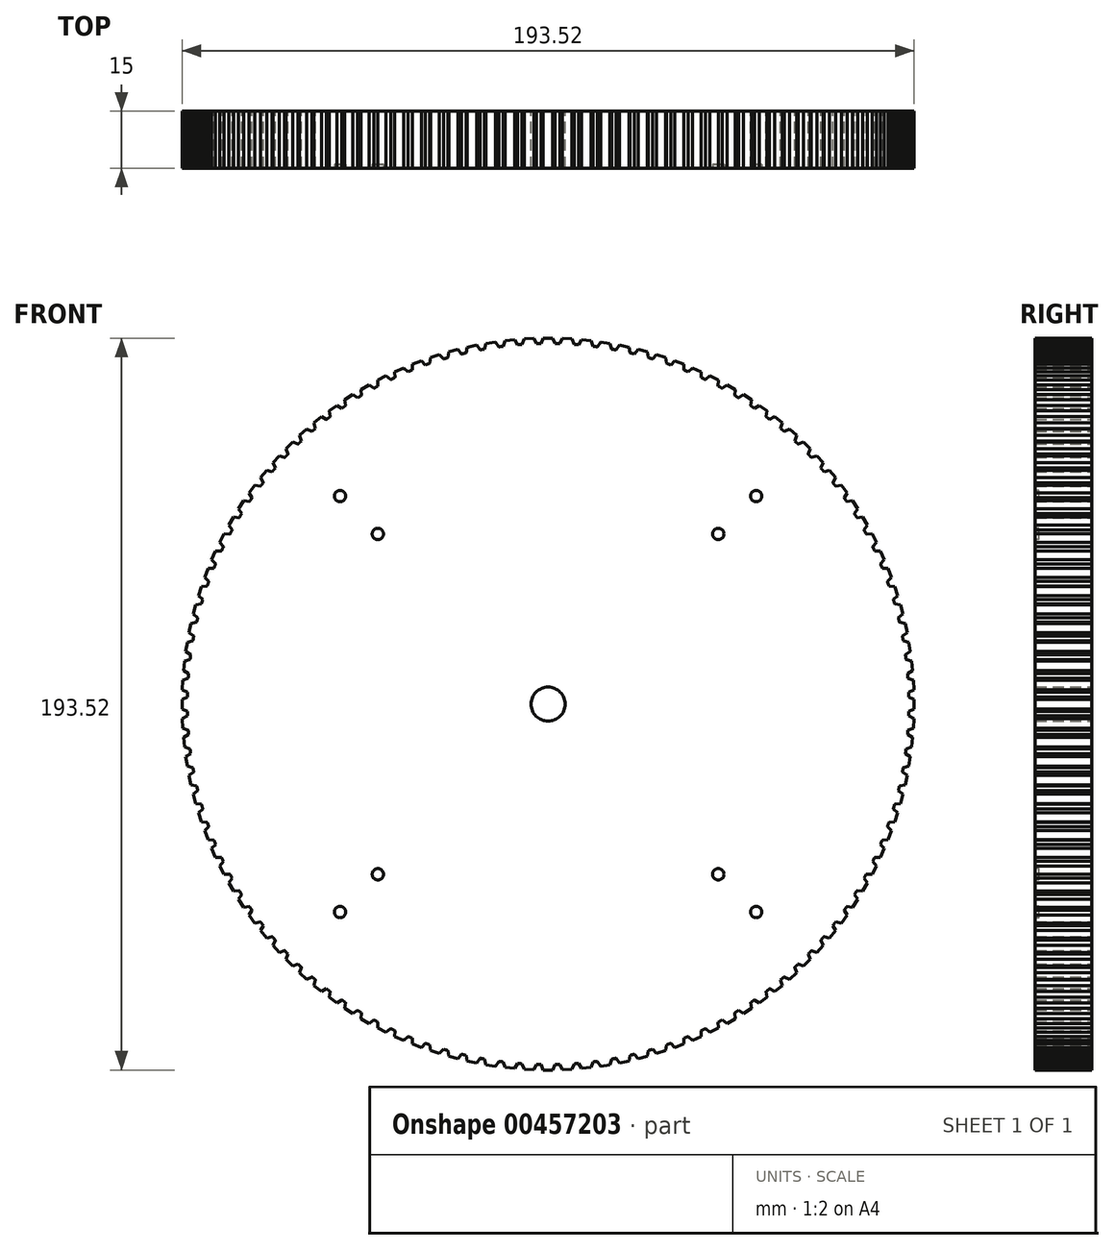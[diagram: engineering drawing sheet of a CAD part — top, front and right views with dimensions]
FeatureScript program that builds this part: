
annotation { "Feature Type Name" : "Feature", "Feature Type Description" : "" }
export const myFeature = defineFeature(function(context is Context, id is Id, definition is map)
    precondition{}
    {
        {
            var Q0;
            Q0=qCreatedBy(makeId("Front.planeOp"),FACE);
            var sketch = newSketch(context, id + "F0", { "sketchPlane" : qUnion([Q0])});
            skCircle(sketch, "E0", {"center": v(0, 0) * mm, "radius": 96.77 * mm, "construction": true});
            skLineSegment(sketch, "E1", {"start": v(0, 96.77) * mm, "end": v(0, 95.37) * mm, "construction": true});
            skCircle(sketch, "E2", {"center": v(0, 0) * mm, "radius": 95.37 * mm});
            skLineSegment(sketch, "E3", {"start": v(0, 0) * mm, "end": v(-1.27, 96.76) * mm, "construction": true});
            skLineSegment(sketch, "E4", {"start": v(0, 0) * mm, "end": v(-2.53, 96.73) * mm, "construction": true});
            skLineSegment(sketch, "E5.MirrorCS", {"start": v(0, 0) * mm, "end": v(1.27, 96.76) * mm, "construction": true});
            skLineSegment(sketch, "E6.MirrorCS", {"start": v(0, 0) * mm, "end": v(2.53, 96.73) * mm, "construction": true});
            skLineSegment(sketch, "E7", {"start": v(-1.27, 96.76) * mm, "end": v(1.27, 96.76) * mm});
            skLineSegment(sketch, "E8", {"start": v(-1.27, 96.76) * mm, "end": v(-1.88, 95.35) * mm});
            skLineSegment(sketch, "E9.MirrorCS", {"start": v(1.27, 96.76) * mm, "end": v(1.88, 95.35) * mm});
            skLineSegment(sketch, "E10.1.0", {"start": v(-6.33, 96.56) * mm, "end": v(-6.87, 95.12) * mm});
            skLineSegment(sketch, "E10.1.1", {"start": v(-6.33, 96.56) * mm, "end": v(-3.8, 96.7) * mm});
            skLineSegment(sketch, "E10.1.2", {"start": v(-3.8, 96.7) * mm, "end": v(-3.11, 95.31) * mm});
            skLineSegment(sketch, "E10.2.0", {"start": v(-11.37, 96.1) * mm, "end": v(-11.84, 94.63) * mm});
            skLineSegment(sketch, "E10.2.1", {"start": v(-11.37, 96.1) * mm, "end": v(-8.85, 96.36) * mm});
            skLineSegment(sketch, "E10.2.2", {"start": v(-8.85, 96.36) * mm, "end": v(-8.1, 95.02) * mm});
            skLineSegment(sketch, "E10.3.0", {"start": v(-16.39, 95.37) * mm, "end": v(-16.77, 93.88) * mm});
            skLineSegment(sketch, "E10.3.1", {"start": v(-16.39, 95.37) * mm, "end": v(-13.89, 95.76) * mm});
            skLineSegment(sketch, "E10.3.2", {"start": v(-13.89, 95.76) * mm, "end": v(-13.06, 94.47) * mm});
            skLineSegment(sketch, "E10.4.0", {"start": v(-21.36, 94.38) * mm, "end": v(-21.66, 92.87) * mm});
            skLineSegment(sketch, "E10.4.1", {"start": v(-21.36, 94.38) * mm, "end": v(-18.88, 94.9) * mm});
            skLineSegment(sketch, "E10.4.2", {"start": v(-18.88, 94.9) * mm, "end": v(-17.98, 93.65) * mm});
            skLineSegment(sketch, "E10.5.0", {"start": v(-26.27, 93.13) * mm, "end": v(-26.5, 91.61) * mm});
            skLineSegment(sketch, "E10.5.1", {"start": v(-26.27, 93.13) * mm, "end": v(-23.82, 93.79) * mm});
            skLineSegment(sketch, "E10.5.2", {"start": v(-23.82, 93.79) * mm, "end": v(-22.86, 92.58) * mm});
            skLineSegment(sketch, "E10.6.0", {"start": v(-31.1, 91.63) * mm, "end": v(-31.25, 90.1) * mm});
            skLineSegment(sketch, "E10.6.1", {"start": v(-31.1, 91.63) * mm, "end": v(-28.7, 92.41) * mm});
            skLineSegment(sketch, "E10.6.2", {"start": v(-28.7, 92.41) * mm, "end": v(-27.68, 91.26) * mm});
            skLineSegment(sketch, "E10.7.0", {"start": v(-35.86, 89.88) * mm, "end": v(-35.92, 88.34) * mm});
            skLineSegment(sketch, "E10.7.1", {"start": v(-35.86, 89.88) * mm, "end": v(-33.5, 90.78) * mm});
            skLineSegment(sketch, "E10.7.2", {"start": v(-33.5, 90.78) * mm, "end": v(-32.41, 89.69) * mm});
            skLineSegment(sketch, "E10.8.0", {"start": v(-40.51, 87.88) * mm, "end": v(-40.5, 86.34) * mm});
            skLineSegment(sketch, "E10.8.1", {"start": v(-40.51, 87.88) * mm, "end": v(-38.2, 88.9) * mm});
            skLineSegment(sketch, "E10.8.2", {"start": v(-38.2, 88.9) * mm, "end": v(-37.06, 87.87) * mm});
            skLineSegment(sketch, "E10.9.0", {"start": v(-45.06, 85.64) * mm, "end": v(-44.96, 84.1) * mm});
            skLineSegment(sketch, "E10.9.1", {"start": v(-45.06, 85.64) * mm, "end": v(-42.8, 86.79) * mm});
            skLineSegment(sketch, "E10.9.2", {"start": v(-42.8, 86.79) * mm, "end": v(-41.61, 85.8) * mm});
            skLineSegment(sketch, "E11", {"start": v(0, 0) * mm, "end": v(0, 96.77) * mm, "construction": true});
            skLineSegment(sketch, "E12.2.10.0", {"start": v(-49.48, 83.16) * mm, "end": v(-49.3, 81.63) * mm});
            skLineSegment(sketch, "E12.3.10.0", {"start": v(-49.48, 83.16) * mm, "end": v(-47.28, 84.43) * mm});
            skLineSegment(sketch, "E12.6.10.0", {"start": v(-47.28, 84.43) * mm, "end": v(-46.05, 83.51) * mm});
            skLineSegment(sketch, "E12.2.11.0", {"start": v(-53.76, 80.46) * mm, "end": v(-53.5, 78.94) * mm});
            skLineSegment(sketch, "E12.3.11.0", {"start": v(-53.76, 80.46) * mm, "end": v(-51.64, 81.84) * mm});
            skLineSegment(sketch, "E12.6.11.0", {"start": v(-51.64, 81.84) * mm, "end": v(-50.35, 80.99) * mm});
            skLineSegment(sketch, "E12.2.12.0", {"start": v(-57.9, 77.53) * mm, "end": v(-57.56, 76.03) * mm});
            skLineSegment(sketch, "E12.3.12.0", {"start": v(-57.9, 77.53) * mm, "end": v(-55.85, 79.02) * mm});
            skLineSegment(sketch, "E12.6.12.0", {"start": v(-55.85, 79.02) * mm, "end": v(-54.52, 78.24) * mm});
            skLineSegment(sketch, "E12.2.13.0", {"start": v(-61.88, 74.4) * mm, "end": v(-61.46, 72.92) * mm});
            skLineSegment(sketch, "E12.3.13.0", {"start": v(-61.88, 74.4) * mm, "end": v(-59.9, 76) * mm});
            skLineSegment(sketch, "E12.6.13.0", {"start": v(-59.9, 76) * mm, "end": v(-58.54, 75.28) * mm});
            skLineSegment(sketch, "E12.2.14.0", {"start": v(-65.68, 71.06) * mm, "end": v(-65.2, 69.6) * mm});
            skLineSegment(sketch, "E12.3.14.0", {"start": v(-65.68, 71.06) * mm, "end": v(-63.8, 72.75) * mm});
            skLineSegment(sketch, "E12.6.14.0", {"start": v(-63.8, 72.75) * mm, "end": v(-62.4, 72.11) * mm});
            skLineSegment(sketch, "E12.2.15.0", {"start": v(-69.31, 67.52) * mm, "end": v(-68.75, 66.1) * mm});
            skLineSegment(sketch, "E12.3.15.0", {"start": v(-69.31, 67.52) * mm, "end": v(-67.52, 69.31) * mm});
            skLineSegment(sketch, "E12.6.15.0", {"start": v(-67.52, 69.31) * mm, "end": v(-66.1, 68.75) * mm});
            skLineSegment(sketch, "E12.2.16.0", {"start": v(-72.75, 63.8) * mm, "end": v(-72.11, 62.4) * mm});
            skLineSegment(sketch, "E12.3.16.0", {"start": v(-72.75, 63.8) * mm, "end": v(-71.06, 65.68) * mm});
            skLineSegment(sketch, "E12.6.16.0", {"start": v(-71.06, 65.68) * mm, "end": v(-69.6, 65.2) * mm});
            skLineSegment(sketch, "E12.2.17.0", {"start": v(-76, 59.9) * mm, "end": v(-75.28, 58.54) * mm});
            skLineSegment(sketch, "E12.3.17.0", {"start": v(-76, 59.9) * mm, "end": v(-74.4, 61.88) * mm});
            skLineSegment(sketch, "E12.6.17.0", {"start": v(-74.4, 61.88) * mm, "end": v(-72.92, 61.46) * mm});
            skLineSegment(sketch, "E12.2.18.0", {"start": v(-79.02, 55.85) * mm, "end": v(-78.24, 54.52) * mm});
            skLineSegment(sketch, "E12.3.18.0", {"start": v(-79.02, 55.85) * mm, "end": v(-77.53, 57.9) * mm});
            skLineSegment(sketch, "E12.6.18.0", {"start": v(-77.53, 57.9) * mm, "end": v(-76.03, 57.56) * mm});
            skLineSegment(sketch, "E12.2.19.0", {"start": v(-81.84, 51.64) * mm, "end": v(-80.99, 50.35) * mm});
            skLineSegment(sketch, "E12.3.19.0", {"start": v(-81.84, 51.64) * mm, "end": v(-80.46, 53.76) * mm});
            skLineSegment(sketch, "E12.6.19.0", {"start": v(-80.46, 53.76) * mm, "end": v(-78.94, 53.5) * mm});
            skLineSegment(sketch, "E12.2.20.0", {"start": v(-84.43, 47.28) * mm, "end": v(-83.51, 46.05) * mm});
            skLineSegment(sketch, "E12.3.20.0", {"start": v(-84.43, 47.28) * mm, "end": v(-83.16, 49.48) * mm});
            skLineSegment(sketch, "E12.6.20.0", {"start": v(-83.16, 49.48) * mm, "end": v(-81.63, 49.3) * mm});
            skLineSegment(sketch, "E12.2.21.0", {"start": v(-86.79, 42.8) * mm, "end": v(-85.8, 41.61) * mm});
            skLineSegment(sketch, "E12.3.21.0", {"start": v(-86.79, 42.8) * mm, "end": v(-85.64, 45.06) * mm});
            skLineSegment(sketch, "E12.6.21.0", {"start": v(-85.64, 45.06) * mm, "end": v(-84.1, 44.96) * mm});
            skLineSegment(sketch, "E12.2.22.0", {"start": v(-88.9, 38.2) * mm, "end": v(-87.87, 37.06) * mm});
            skLineSegment(sketch, "E12.3.22.0", {"start": v(-88.9, 38.2) * mm, "end": v(-87.88, 40.51) * mm});
            skLineSegment(sketch, "E12.6.22.0", {"start": v(-87.88, 40.51) * mm, "end": v(-86.34, 40.5) * mm});
            skLineSegment(sketch, "E12.2.23.0", {"start": v(-90.78, 33.5) * mm, "end": v(-89.69, 32.41) * mm});
            skLineSegment(sketch, "E12.3.23.0", {"start": v(-90.78, 33.5) * mm, "end": v(-89.88, 35.86) * mm});
            skLineSegment(sketch, "E12.6.23.0", {"start": v(-89.88, 35.86) * mm, "end": v(-88.34, 35.92) * mm});
            skLineSegment(sketch, "E12.2.24.0", {"start": v(-92.41, 28.7) * mm, "end": v(-91.26, 27.68) * mm});
            skLineSegment(sketch, "E12.3.24.0", {"start": v(-92.41, 28.7) * mm, "end": v(-91.63, 31.1) * mm});
            skLineSegment(sketch, "E12.6.24.0", {"start": v(-91.63, 31.1) * mm, "end": v(-90.1, 31.25) * mm});
            skLineSegment(sketch, "E12.2.25.0", {"start": v(-93.79, 23.82) * mm, "end": v(-92.58, 22.86) * mm});
            skLineSegment(sketch, "E12.3.25.0", {"start": v(-93.79, 23.82) * mm, "end": v(-93.13, 26.27) * mm});
            skLineSegment(sketch, "E12.6.25.0", {"start": v(-93.13, 26.27) * mm, "end": v(-91.61, 26.5) * mm});
            skLineSegment(sketch, "E12.2.26.0", {"start": v(-94.9, 18.88) * mm, "end": v(-93.65, 17.98) * mm});
            skLineSegment(sketch, "E12.3.26.0", {"start": v(-94.9, 18.88) * mm, "end": v(-94.38, 21.36) * mm});
            skLineSegment(sketch, "E12.6.26.0", {"start": v(-94.38, 21.36) * mm, "end": v(-92.87, 21.66) * mm});
            skLineSegment(sketch, "E12.2.27.0", {"start": v(-95.76, 13.89) * mm, "end": v(-94.47, 13.06) * mm});
            skLineSegment(sketch, "E12.3.27.0", {"start": v(-95.76, 13.89) * mm, "end": v(-95.37, 16.39) * mm});
            skLineSegment(sketch, "E12.6.27.0", {"start": v(-95.37, 16.39) * mm, "end": v(-93.88, 16.77) * mm});
            skLineSegment(sketch, "E12.2.28.0", {"start": v(-96.36, 8.85) * mm, "end": v(-95.02, 8.1) * mm});
            skLineSegment(sketch, "E12.3.28.0", {"start": v(-96.36, 8.85) * mm, "end": v(-96.1, 11.37) * mm});
            skLineSegment(sketch, "E12.6.28.0", {"start": v(-96.1, 11.37) * mm, "end": v(-94.63, 11.84) * mm});
            skLineSegment(sketch, "E12.2.29.0", {"start": v(-96.7, 3.8) * mm, "end": v(-95.31, 3.11) * mm});
            skLineSegment(sketch, "E12.3.29.0", {"start": v(-96.7, 3.8) * mm, "end": v(-96.56, 6.33) * mm});
            skLineSegment(sketch, "E12.6.29.0", {"start": v(-96.56, 6.33) * mm, "end": v(-95.12, 6.87) * mm});
            skLineSegment(sketch, "E12.2.30.0", {"start": v(-96.76, -1.27) * mm, "end": v(-95.35, -1.88) * mm});
            skLineSegment(sketch, "E12.3.30.0", {"start": v(-96.76, -1.27) * mm, "end": v(-96.76, 1.27) * mm});
            skLineSegment(sketch, "E12.6.30.0", {"start": v(-96.76, 1.27) * mm, "end": v(-95.35, 1.88) * mm});
            skLineSegment(sketch, "E12.2.31.0", {"start": v(-96.56, -6.33) * mm, "end": v(-95.12, -6.87) * mm});
            skLineSegment(sketch, "E12.3.31.0", {"start": v(-96.56, -6.33) * mm, "end": v(-96.7, -3.8) * mm});
            skLineSegment(sketch, "E12.6.31.0", {"start": v(-96.7, -3.8) * mm, "end": v(-95.31, -3.11) * mm});
            skLineSegment(sketch, "E12.2.32.0", {"start": v(-96.1, -11.37) * mm, "end": v(-94.63, -11.84) * mm});
            skLineSegment(sketch, "E12.3.32.0", {"start": v(-96.1, -11.37) * mm, "end": v(-96.36, -8.85) * mm});
            skLineSegment(sketch, "E12.6.32.0", {"start": v(-96.36, -8.85) * mm, "end": v(-95.02, -8.1) * mm});
            skLineSegment(sketch, "E12.2.33.0", {"start": v(-95.37, -16.39) * mm, "end": v(-93.88, -16.77) * mm});
            skLineSegment(sketch, "E12.3.33.0", {"start": v(-95.37, -16.39) * mm, "end": v(-95.76, -13.89) * mm});
            skLineSegment(sketch, "E12.6.33.0", {"start": v(-95.76, -13.89) * mm, "end": v(-94.47, -13.06) * mm});
            skLineSegment(sketch, "E12.2.34.0", {"start": v(-94.38, -21.36) * mm, "end": v(-92.87, -21.66) * mm});
            skLineSegment(sketch, "E12.3.34.0", {"start": v(-94.38, -21.36) * mm, "end": v(-94.9, -18.88) * mm});
            skLineSegment(sketch, "E12.6.34.0", {"start": v(-94.9, -18.88) * mm, "end": v(-93.65, -17.98) * mm});
            skLineSegment(sketch, "E12.2.35.0", {"start": v(-93.13, -26.27) * mm, "end": v(-91.61, -26.5) * mm});
            skLineSegment(sketch, "E12.3.35.0", {"start": v(-93.13, -26.27) * mm, "end": v(-93.79, -23.82) * mm});
            skLineSegment(sketch, "E12.6.35.0", {"start": v(-93.79, -23.82) * mm, "end": v(-92.58, -22.86) * mm});
            skLineSegment(sketch, "E12.2.36.0", {"start": v(-91.63, -31.1) * mm, "end": v(-90.1, -31.25) * mm});
            skLineSegment(sketch, "E12.3.36.0", {"start": v(-91.63, -31.1) * mm, "end": v(-92.41, -28.7) * mm});
            skLineSegment(sketch, "E12.6.36.0", {"start": v(-92.41, -28.7) * mm, "end": v(-91.26, -27.68) * mm});
            skLineSegment(sketch, "E12.2.37.0", {"start": v(-89.88, -35.86) * mm, "end": v(-88.34, -35.92) * mm});
            skLineSegment(sketch, "E12.3.37.0", {"start": v(-89.88, -35.86) * mm, "end": v(-90.78, -33.5) * mm});
            skLineSegment(sketch, "E12.6.37.0", {"start": v(-90.78, -33.5) * mm, "end": v(-89.69, -32.41) * mm});
            skLineSegment(sketch, "E12.2.38.0", {"start": v(-87.88, -40.51) * mm, "end": v(-86.34, -40.5) * mm});
            skLineSegment(sketch, "E12.3.38.0", {"start": v(-87.88, -40.51) * mm, "end": v(-88.9, -38.2) * mm});
            skLineSegment(sketch, "E12.6.38.0", {"start": v(-88.9, -38.2) * mm, "end": v(-87.87, -37.06) * mm});
            skLineSegment(sketch, "E12.2.39.0", {"start": v(-85.64, -45.06) * mm, "end": v(-84.1, -44.96) * mm});
            skLineSegment(sketch, "E12.3.39.0", {"start": v(-85.64, -45.06) * mm, "end": v(-86.79, -42.8) * mm});
            skLineSegment(sketch, "E12.6.39.0", {"start": v(-86.79, -42.8) * mm, "end": v(-85.8, -41.61) * mm});
            skLineSegment(sketch, "E12.2.40.0", {"start": v(-83.16, -49.48) * mm, "end": v(-81.63, -49.3) * mm});
            skLineSegment(sketch, "E12.3.40.0", {"start": v(-83.16, -49.48) * mm, "end": v(-84.43, -47.28) * mm});
            skLineSegment(sketch, "E12.6.40.0", {"start": v(-84.43, -47.28) * mm, "end": v(-83.51, -46.05) * mm});
            skLineSegment(sketch, "E12.2.41.0", {"start": v(-80.46, -53.76) * mm, "end": v(-78.94, -53.5) * mm});
            skLineSegment(sketch, "E12.3.41.0", {"start": v(-80.46, -53.76) * mm, "end": v(-81.84, -51.64) * mm});
            skLineSegment(sketch, "E12.6.41.0", {"start": v(-81.84, -51.64) * mm, "end": v(-80.99, -50.35) * mm});
            skLineSegment(sketch, "E12.2.42.0", {"start": v(-77.53, -57.9) * mm, "end": v(-76.03, -57.56) * mm});
            skLineSegment(sketch, "E12.3.42.0", {"start": v(-77.53, -57.9) * mm, "end": v(-79.02, -55.85) * mm});
            skLineSegment(sketch, "E12.6.42.0", {"start": v(-79.02, -55.85) * mm, "end": v(-78.24, -54.52) * mm});
            skLineSegment(sketch, "E12.2.43.0", {"start": v(-74.4, -61.88) * mm, "end": v(-72.92, -61.46) * mm});
            skLineSegment(sketch, "E12.3.43.0", {"start": v(-74.4, -61.88) * mm, "end": v(-76, -59.9) * mm});
            skLineSegment(sketch, "E12.6.43.0", {"start": v(-76, -59.9) * mm, "end": v(-75.28, -58.54) * mm});
            skLineSegment(sketch, "E12.2.44.0", {"start": v(-71.06, -65.68) * mm, "end": v(-69.6, -65.2) * mm});
            skLineSegment(sketch, "E12.3.44.0", {"start": v(-71.06, -65.68) * mm, "end": v(-72.75, -63.8) * mm});
            skLineSegment(sketch, "E12.6.44.0", {"start": v(-72.75, -63.8) * mm, "end": v(-72.11, -62.4) * mm});
            skLineSegment(sketch, "E12.2.45.0", {"start": v(-67.52, -69.31) * mm, "end": v(-66.1, -68.75) * mm});
            skLineSegment(sketch, "E12.3.45.0", {"start": v(-67.52, -69.31) * mm, "end": v(-69.31, -67.52) * mm});
            skLineSegment(sketch, "E12.6.45.0", {"start": v(-69.31, -67.52) * mm, "end": v(-68.75, -66.1) * mm});
            skLineSegment(sketch, "E12.2.46.0", {"start": v(-63.8, -72.75) * mm, "end": v(-62.4, -72.11) * mm});
            skLineSegment(sketch, "E12.3.46.0", {"start": v(-63.8, -72.75) * mm, "end": v(-65.68, -71.06) * mm});
            skLineSegment(sketch, "E12.6.46.0", {"start": v(-65.68, -71.06) * mm, "end": v(-65.2, -69.6) * mm});
            skLineSegment(sketch, "E12.2.47.0", {"start": v(-59.9, -76) * mm, "end": v(-58.54, -75.28) * mm});
            skLineSegment(sketch, "E12.3.47.0", {"start": v(-59.9, -76) * mm, "end": v(-61.88, -74.4) * mm});
            skLineSegment(sketch, "E12.6.47.0", {"start": v(-61.88, -74.4) * mm, "end": v(-61.46, -72.92) * mm});
            skLineSegment(sketch, "E12.2.48.0", {"start": v(-55.85, -79.02) * mm, "end": v(-54.52, -78.24) * mm});
            skLineSegment(sketch, "E12.3.48.0", {"start": v(-55.85, -79.02) * mm, "end": v(-57.9, -77.53) * mm});
            skLineSegment(sketch, "E12.6.48.0", {"start": v(-57.9, -77.53) * mm, "end": v(-57.56, -76.03) * mm});
            skLineSegment(sketch, "E12.2.49.0", {"start": v(-51.64, -81.84) * mm, "end": v(-50.35, -80.99) * mm});
            skLineSegment(sketch, "E12.3.49.0", {"start": v(-51.64, -81.84) * mm, "end": v(-53.76, -80.46) * mm});
            skLineSegment(sketch, "E12.6.49.0", {"start": v(-53.76, -80.46) * mm, "end": v(-53.5, -78.94) * mm});
            skLineSegment(sketch, "E12.2.50.0", {"start": v(-47.28, -84.43) * mm, "end": v(-46.05, -83.51) * mm});
            skLineSegment(sketch, "E12.3.50.0", {"start": v(-47.28, -84.43) * mm, "end": v(-49.48, -83.16) * mm});
            skLineSegment(sketch, "E12.6.50.0", {"start": v(-49.48, -83.16) * mm, "end": v(-49.3, -81.63) * mm});
            skLineSegment(sketch, "E12.2.51.0", {"start": v(-42.8, -86.79) * mm, "end": v(-41.61, -85.8) * mm});
            skLineSegment(sketch, "E12.3.51.0", {"start": v(-42.8, -86.79) * mm, "end": v(-45.06, -85.64) * mm});
            skLineSegment(sketch, "E12.6.51.0", {"start": v(-45.06, -85.64) * mm, "end": v(-44.96, -84.1) * mm});
            skLineSegment(sketch, "E12.2.52.0", {"start": v(-38.2, -88.9) * mm, "end": v(-37.06, -87.87) * mm});
            skLineSegment(sketch, "E12.3.52.0", {"start": v(-38.2, -88.9) * mm, "end": v(-40.51, -87.88) * mm});
            skLineSegment(sketch, "E12.6.52.0", {"start": v(-40.51, -87.88) * mm, "end": v(-40.5, -86.34) * mm});
            skLineSegment(sketch, "E12.2.53.0", {"start": v(-33.5, -90.78) * mm, "end": v(-32.41, -89.69) * mm});
            skLineSegment(sketch, "E12.3.53.0", {"start": v(-33.5, -90.78) * mm, "end": v(-35.86, -89.88) * mm});
            skLineSegment(sketch, "E12.6.53.0", {"start": v(-35.86, -89.88) * mm, "end": v(-35.92, -88.34) * mm});
            skLineSegment(sketch, "E12.2.54.0", {"start": v(-28.7, -92.41) * mm, "end": v(-27.68, -91.26) * mm});
            skLineSegment(sketch, "E12.3.54.0", {"start": v(-28.7, -92.41) * mm, "end": v(-31.1, -91.63) * mm});
            skLineSegment(sketch, "E12.6.54.0", {"start": v(-31.1, -91.63) * mm, "end": v(-31.25, -90.1) * mm});
            skLineSegment(sketch, "E12.2.55.0", {"start": v(-23.82, -93.79) * mm, "end": v(-22.86, -92.58) * mm});
            skLineSegment(sketch, "E12.3.55.0", {"start": v(-23.82, -93.79) * mm, "end": v(-26.27, -93.13) * mm});
            skLineSegment(sketch, "E12.6.55.0", {"start": v(-26.27, -93.13) * mm, "end": v(-26.5, -91.61) * mm});
            skLineSegment(sketch, "E12.2.56.0", {"start": v(-18.88, -94.9) * mm, "end": v(-17.98, -93.65) * mm});
            skLineSegment(sketch, "E12.3.56.0", {"start": v(-18.88, -94.9) * mm, "end": v(-21.36, -94.38) * mm});
            skLineSegment(sketch, "E12.6.56.0", {"start": v(-21.36, -94.38) * mm, "end": v(-21.66, -92.87) * mm});
            skLineSegment(sketch, "E12.2.57.0", {"start": v(-13.89, -95.76) * mm, "end": v(-13.06, -94.47) * mm});
            skLineSegment(sketch, "E12.3.57.0", {"start": v(-13.89, -95.76) * mm, "end": v(-16.39, -95.37) * mm});
            skLineSegment(sketch, "E12.6.57.0", {"start": v(-16.39, -95.37) * mm, "end": v(-16.77, -93.88) * mm});
            skLineSegment(sketch, "E12.2.58.0", {"start": v(-8.85, -96.36) * mm, "end": v(-8.1, -95.02) * mm});
            skLineSegment(sketch, "E12.3.58.0", {"start": v(-8.85, -96.36) * mm, "end": v(-11.37, -96.1) * mm});
            skLineSegment(sketch, "E12.6.58.0", {"start": v(-11.37, -96.1) * mm, "end": v(-11.84, -94.63) * mm});
            skLineSegment(sketch, "E12.2.59.0", {"start": v(-3.8, -96.7) * mm, "end": v(-3.11, -95.31) * mm});
            skLineSegment(sketch, "E12.3.59.0", {"start": v(-3.8, -96.7) * mm, "end": v(-6.33, -96.56) * mm});
            skLineSegment(sketch, "E12.6.59.0", {"start": v(-6.33, -96.56) * mm, "end": v(-6.87, -95.12) * mm});
            skLineSegment(sketch, "E13.2.60.0", {"start": v(1.27, -96.76) * mm, "end": v(1.88, -95.35) * mm});
            skLineSegment(sketch, "E13.3.60.0", {"start": v(1.27, -96.76) * mm, "end": v(-1.27, -96.76) * mm});
            skLineSegment(sketch, "E13.6.60.0", {"start": v(-1.27, -96.76) * mm, "end": v(-1.88, -95.35) * mm});
            skLineSegment(sketch, "E13.2.61.0", {"start": v(6.33, -96.56) * mm, "end": v(6.87, -95.12) * mm});
            skLineSegment(sketch, "E13.3.61.0", {"start": v(6.33, -96.56) * mm, "end": v(3.8, -96.7) * mm});
            skLineSegment(sketch, "E13.6.61.0", {"start": v(3.8, -96.7) * mm, "end": v(3.11, -95.31) * mm});
            skLineSegment(sketch, "E13.2.62.0", {"start": v(11.37, -96.1) * mm, "end": v(11.84, -94.63) * mm});
            skLineSegment(sketch, "E13.3.62.0", {"start": v(11.37, -96.1) * mm, "end": v(8.85, -96.36) * mm});
            skLineSegment(sketch, "E13.6.62.0", {"start": v(8.85, -96.36) * mm, "end": v(8.1, -95.02) * mm});
            skLineSegment(sketch, "E13.2.63.0", {"start": v(16.39, -95.37) * mm, "end": v(16.77, -93.88) * mm});
            skLineSegment(sketch, "E13.3.63.0", {"start": v(16.39, -95.37) * mm, "end": v(13.89, -95.76) * mm});
            skLineSegment(sketch, "E13.6.63.0", {"start": v(13.89, -95.76) * mm, "end": v(13.06, -94.47) * mm});
            skLineSegment(sketch, "E13.2.64.0", {"start": v(21.36, -94.38) * mm, "end": v(21.66, -92.87) * mm});
            skLineSegment(sketch, "E13.3.64.0", {"start": v(21.36, -94.38) * mm, "end": v(18.88, -94.9) * mm});
            skLineSegment(sketch, "E13.6.64.0", {"start": v(18.88, -94.9) * mm, "end": v(17.98, -93.65) * mm});
            skLineSegment(sketch, "E13.2.65.0", {"start": v(26.27, -93.13) * mm, "end": v(26.5, -91.61) * mm});
            skLineSegment(sketch, "E13.3.65.0", {"start": v(26.27, -93.13) * mm, "end": v(23.82, -93.79) * mm});
            skLineSegment(sketch, "E13.6.65.0", {"start": v(23.82, -93.79) * mm, "end": v(22.86, -92.58) * mm});
            skLineSegment(sketch, "E13.2.66.0", {"start": v(31.1, -91.63) * mm, "end": v(31.25, -90.1) * mm});
            skLineSegment(sketch, "E13.3.66.0", {"start": v(31.1, -91.63) * mm, "end": v(28.7, -92.41) * mm});
            skLineSegment(sketch, "E13.6.66.0", {"start": v(28.7, -92.41) * mm, "end": v(27.68, -91.26) * mm});
            skLineSegment(sketch, "E13.2.67.0", {"start": v(35.86, -89.88) * mm, "end": v(35.92, -88.34) * mm});
            skLineSegment(sketch, "E13.3.67.0", {"start": v(35.86, -89.88) * mm, "end": v(33.5, -90.78) * mm});
            skLineSegment(sketch, "E13.6.67.0", {"start": v(33.5, -90.78) * mm, "end": v(32.41, -89.69) * mm});
            skLineSegment(sketch, "E13.2.68.0", {"start": v(40.51, -87.88) * mm, "end": v(40.5, -86.34) * mm});
            skLineSegment(sketch, "E13.3.68.0", {"start": v(40.51, -87.88) * mm, "end": v(38.2, -88.9) * mm});
            skLineSegment(sketch, "E13.6.68.0", {"start": v(38.2, -88.9) * mm, "end": v(37.06, -87.87) * mm});
            skLineSegment(sketch, "E13.2.69.0", {"start": v(45.06, -85.64) * mm, "end": v(44.96, -84.1) * mm});
            skLineSegment(sketch, "E13.3.69.0", {"start": v(45.06, -85.64) * mm, "end": v(42.8, -86.79) * mm});
            skLineSegment(sketch, "E13.6.69.0", {"start": v(42.8, -86.79) * mm, "end": v(41.61, -85.8) * mm});
            skLineSegment(sketch, "E13.2.70.0", {"start": v(49.48, -83.16) * mm, "end": v(49.3, -81.63) * mm});
            skLineSegment(sketch, "E13.3.70.0", {"start": v(49.48, -83.16) * mm, "end": v(47.28, -84.43) * mm});
            skLineSegment(sketch, "E13.6.70.0", {"start": v(47.28, -84.43) * mm, "end": v(46.05, -83.51) * mm});
            skLineSegment(sketch, "E13.2.71.0", {"start": v(53.76, -80.46) * mm, "end": v(53.5, -78.94) * mm});
            skLineSegment(sketch, "E13.3.71.0", {"start": v(53.76, -80.46) * mm, "end": v(51.64, -81.84) * mm});
            skLineSegment(sketch, "E13.6.71.0", {"start": v(51.64, -81.84) * mm, "end": v(50.35, -80.99) * mm});
            skLineSegment(sketch, "E13.2.72.0", {"start": v(57.9, -77.53) * mm, "end": v(57.56, -76.03) * mm});
            skLineSegment(sketch, "E13.3.72.0", {"start": v(57.9, -77.53) * mm, "end": v(55.85, -79.02) * mm});
            skLineSegment(sketch, "E13.6.72.0", {"start": v(55.85, -79.02) * mm, "end": v(54.52, -78.24) * mm});
            skLineSegment(sketch, "E13.2.73.0", {"start": v(61.88, -74.4) * mm, "end": v(61.46, -72.92) * mm});
            skLineSegment(sketch, "E13.3.73.0", {"start": v(61.88, -74.4) * mm, "end": v(59.9, -76) * mm});
            skLineSegment(sketch, "E13.6.73.0", {"start": v(59.9, -76) * mm, "end": v(58.54, -75.28) * mm});
            skLineSegment(sketch, "E13.2.74.0", {"start": v(65.68, -71.06) * mm, "end": v(65.2, -69.6) * mm});
            skLineSegment(sketch, "E13.3.74.0", {"start": v(65.68, -71.06) * mm, "end": v(63.8, -72.75) * mm});
            skLineSegment(sketch, "E13.6.74.0", {"start": v(63.8, -72.75) * mm, "end": v(62.4, -72.11) * mm});
            skLineSegment(sketch, "E13.2.75.0", {"start": v(69.31, -67.52) * mm, "end": v(68.75, -66.1) * mm});
            skLineSegment(sketch, "E13.3.75.0", {"start": v(69.31, -67.52) * mm, "end": v(67.52, -69.31) * mm});
            skLineSegment(sketch, "E13.6.75.0", {"start": v(67.52, -69.31) * mm, "end": v(66.1, -68.75) * mm});
            skLineSegment(sketch, "E13.2.76.0", {"start": v(72.75, -63.8) * mm, "end": v(72.11, -62.4) * mm});
            skLineSegment(sketch, "E13.3.76.0", {"start": v(72.75, -63.8) * mm, "end": v(71.06, -65.68) * mm});
            skLineSegment(sketch, "E13.6.76.0", {"start": v(71.06, -65.68) * mm, "end": v(69.6, -65.2) * mm});
            skLineSegment(sketch, "E13.2.77.0", {"start": v(76, -59.9) * mm, "end": v(75.28, -58.54) * mm});
            skLineSegment(sketch, "E13.3.77.0", {"start": v(76, -59.9) * mm, "end": v(74.4, -61.88) * mm});
            skLineSegment(sketch, "E13.6.77.0", {"start": v(74.4, -61.88) * mm, "end": v(72.92, -61.46) * mm});
            skLineSegment(sketch, "E13.2.78.0", {"start": v(79.02, -55.85) * mm, "end": v(78.24, -54.52) * mm});
            skLineSegment(sketch, "E13.3.78.0", {"start": v(79.02, -55.85) * mm, "end": v(77.53, -57.9) * mm});
            skLineSegment(sketch, "E13.6.78.0", {"start": v(77.53, -57.9) * mm, "end": v(76.03, -57.56) * mm});
            skLineSegment(sketch, "E13.2.79.0", {"start": v(81.84, -51.64) * mm, "end": v(80.99, -50.35) * mm});
            skLineSegment(sketch, "E13.3.79.0", {"start": v(81.84, -51.64) * mm, "end": v(80.46, -53.76) * mm});
            skLineSegment(sketch, "E13.6.79.0", {"start": v(80.46, -53.76) * mm, "end": v(78.94, -53.5) * mm});
            skLineSegment(sketch, "E13.2.80.0", {"start": v(84.43, -47.28) * mm, "end": v(83.51, -46.05) * mm});
            skLineSegment(sketch, "E13.3.80.0", {"start": v(84.43, -47.28) * mm, "end": v(83.16, -49.48) * mm});
            skLineSegment(sketch, "E13.6.80.0", {"start": v(83.16, -49.48) * mm, "end": v(81.63, -49.3) * mm});
            skLineSegment(sketch, "E13.2.81.0", {"start": v(86.79, -42.8) * mm, "end": v(85.8, -41.61) * mm});
            skLineSegment(sketch, "E13.3.81.0", {"start": v(86.79, -42.8) * mm, "end": v(85.64, -45.06) * mm});
            skLineSegment(sketch, "E13.6.81.0", {"start": v(85.64, -45.06) * mm, "end": v(84.1, -44.96) * mm});
            skLineSegment(sketch, "E13.2.82.0", {"start": v(88.9, -38.2) * mm, "end": v(87.87, -37.06) * mm});
            skLineSegment(sketch, "E13.3.82.0", {"start": v(88.9, -38.2) * mm, "end": v(87.88, -40.51) * mm});
            skLineSegment(sketch, "E13.6.82.0", {"start": v(87.88, -40.51) * mm, "end": v(86.34, -40.5) * mm});
            skLineSegment(sketch, "E13.2.83.0", {"start": v(90.78, -33.5) * mm, "end": v(89.69, -32.41) * mm});
            skLineSegment(sketch, "E13.3.83.0", {"start": v(90.78, -33.5) * mm, "end": v(89.88, -35.86) * mm});
            skLineSegment(sketch, "E13.6.83.0", {"start": v(89.88, -35.86) * mm, "end": v(88.34, -35.92) * mm});
            skLineSegment(sketch, "E13.2.84.0", {"start": v(92.41, -28.7) * mm, "end": v(91.26, -27.68) * mm});
            skLineSegment(sketch, "E13.3.84.0", {"start": v(92.41, -28.7) * mm, "end": v(91.63, -31.1) * mm});
            skLineSegment(sketch, "E13.6.84.0", {"start": v(91.63, -31.1) * mm, "end": v(90.1, -31.25) * mm});
            skLineSegment(sketch, "E13.2.85.0", {"start": v(93.79, -23.82) * mm, "end": v(92.58, -22.86) * mm});
            skLineSegment(sketch, "E13.3.85.0", {"start": v(93.79, -23.82) * mm, "end": v(93.13, -26.27) * mm});
            skLineSegment(sketch, "E13.6.85.0", {"start": v(93.13, -26.27) * mm, "end": v(91.61, -26.5) * mm});
            skLineSegment(sketch, "E13.2.86.0", {"start": v(94.9, -18.88) * mm, "end": v(93.65, -17.98) * mm});
            skLineSegment(sketch, "E13.3.86.0", {"start": v(94.9, -18.88) * mm, "end": v(94.38, -21.36) * mm});
            skLineSegment(sketch, "E13.6.86.0", {"start": v(94.38, -21.36) * mm, "end": v(92.87, -21.66) * mm});
            skLineSegment(sketch, "E13.2.87.0", {"start": v(95.76, -13.89) * mm, "end": v(94.47, -13.06) * mm});
            skLineSegment(sketch, "E13.3.87.0", {"start": v(95.76, -13.89) * mm, "end": v(95.37, -16.39) * mm});
            skLineSegment(sketch, "E13.6.87.0", {"start": v(95.37, -16.39) * mm, "end": v(93.88, -16.77) * mm});
            skLineSegment(sketch, "E13.2.88.0", {"start": v(96.36, -8.85) * mm, "end": v(95.02, -8.1) * mm});
            skLineSegment(sketch, "E13.3.88.0", {"start": v(96.36, -8.85) * mm, "end": v(96.1, -11.37) * mm});
            skLineSegment(sketch, "E13.6.88.0", {"start": v(96.1, -11.37) * mm, "end": v(94.63, -11.84) * mm});
            skLineSegment(sketch, "E13.2.89.0", {"start": v(96.7, -3.8) * mm, "end": v(95.31, -3.11) * mm});
            skLineSegment(sketch, "E13.3.89.0", {"start": v(96.7, -3.8) * mm, "end": v(96.56, -6.33) * mm});
            skLineSegment(sketch, "E13.6.89.0", {"start": v(96.56, -6.33) * mm, "end": v(95.12, -6.87) * mm});
            skLineSegment(sketch, "E13.2.90.0", {"start": v(96.76, 1.27) * mm, "end": v(95.35, 1.88) * mm});
            skLineSegment(sketch, "E13.3.90.0", {"start": v(96.76, 1.27) * mm, "end": v(96.76, -1.27) * mm});
            skLineSegment(sketch, "E13.6.90.0", {"start": v(96.76, -1.27) * mm, "end": v(95.35, -1.88) * mm});
            skLineSegment(sketch, "E13.2.91.0", {"start": v(96.56, 6.33) * mm, "end": v(95.12, 6.87) * mm});
            skLineSegment(sketch, "E13.3.91.0", {"start": v(96.56, 6.33) * mm, "end": v(96.7, 3.8) * mm});
            skLineSegment(sketch, "E13.6.91.0", {"start": v(96.7, 3.8) * mm, "end": v(95.31, 3.11) * mm});
            skLineSegment(sketch, "E13.2.92.0", {"start": v(96.1, 11.37) * mm, "end": v(94.63, 11.84) * mm});
            skLineSegment(sketch, "E13.3.92.0", {"start": v(96.1, 11.37) * mm, "end": v(96.36, 8.85) * mm});
            skLineSegment(sketch, "E13.6.92.0", {"start": v(96.36, 8.85) * mm, "end": v(95.02, 8.1) * mm});
            skLineSegment(sketch, "E13.2.93.0", {"start": v(95.37, 16.39) * mm, "end": v(93.88, 16.77) * mm});
            skLineSegment(sketch, "E13.3.93.0", {"start": v(95.37, 16.39) * mm, "end": v(95.76, 13.89) * mm});
            skLineSegment(sketch, "E13.6.93.0", {"start": v(95.76, 13.89) * mm, "end": v(94.47, 13.06) * mm});
            skLineSegment(sketch, "E13.2.94.0", {"start": v(94.38, 21.36) * mm, "end": v(92.87, 21.66) * mm});
            skLineSegment(sketch, "E13.3.94.0", {"start": v(94.38, 21.36) * mm, "end": v(94.9, 18.88) * mm});
            skLineSegment(sketch, "E13.6.94.0", {"start": v(94.9, 18.88) * mm, "end": v(93.65, 17.98) * mm});
            skLineSegment(sketch, "E13.2.95.0", {"start": v(93.13, 26.27) * mm, "end": v(91.61, 26.5) * mm});
            skLineSegment(sketch, "E13.3.95.0", {"start": v(93.13, 26.27) * mm, "end": v(93.79, 23.82) * mm});
            skLineSegment(sketch, "E13.6.95.0", {"start": v(93.79, 23.82) * mm, "end": v(92.58, 22.86) * mm});
            skLineSegment(sketch, "E13.2.96.0", {"start": v(91.63, 31.1) * mm, "end": v(90.1, 31.25) * mm});
            skLineSegment(sketch, "E13.3.96.0", {"start": v(91.63, 31.1) * mm, "end": v(92.41, 28.7) * mm});
            skLineSegment(sketch, "E13.6.96.0", {"start": v(92.41, 28.7) * mm, "end": v(91.26, 27.68) * mm});
            skLineSegment(sketch, "E13.2.97.0", {"start": v(89.88, 35.86) * mm, "end": v(88.34, 35.92) * mm});
            skLineSegment(sketch, "E13.3.97.0", {"start": v(89.88, 35.86) * mm, "end": v(90.78, 33.5) * mm});
            skLineSegment(sketch, "E13.6.97.0", {"start": v(90.78, 33.5) * mm, "end": v(89.69, 32.41) * mm});
            skLineSegment(sketch, "E13.2.98.0", {"start": v(87.88, 40.51) * mm, "end": v(86.34, 40.5) * mm});
            skLineSegment(sketch, "E13.3.98.0", {"start": v(87.88, 40.51) * mm, "end": v(88.9, 38.2) * mm});
            skLineSegment(sketch, "E13.6.98.0", {"start": v(88.9, 38.2) * mm, "end": v(87.87, 37.06) * mm});
            skLineSegment(sketch, "E13.2.99.0", {"start": v(85.64, 45.06) * mm, "end": v(84.1, 44.96) * mm});
            skLineSegment(sketch, "E13.3.99.0", {"start": v(85.64, 45.06) * mm, "end": v(86.79, 42.8) * mm});
            skLineSegment(sketch, "E13.6.99.0", {"start": v(86.79, 42.8) * mm, "end": v(85.8, 41.61) * mm});
            skLineSegment(sketch, "E13.2.100.0", {"start": v(83.16, 49.48) * mm, "end": v(81.63, 49.3) * mm});
            skLineSegment(sketch, "E13.3.100.0", {"start": v(83.16, 49.48) * mm, "end": v(84.43, 47.28) * mm});
            skLineSegment(sketch, "E13.6.100.0", {"start": v(84.43, 47.28) * mm, "end": v(83.51, 46.05) * mm});
            skLineSegment(sketch, "E13.2.101.0", {"start": v(80.46, 53.76) * mm, "end": v(78.94, 53.5) * mm});
            skLineSegment(sketch, "E13.3.101.0", {"start": v(80.46, 53.76) * mm, "end": v(81.84, 51.64) * mm});
            skLineSegment(sketch, "E13.6.101.0", {"start": v(81.84, 51.64) * mm, "end": v(80.99, 50.35) * mm});
            skLineSegment(sketch, "E13.2.102.0", {"start": v(77.53, 57.9) * mm, "end": v(76.03, 57.56) * mm});
            skLineSegment(sketch, "E13.3.102.0", {"start": v(77.53, 57.9) * mm, "end": v(79.02, 55.85) * mm});
            skLineSegment(sketch, "E13.6.102.0", {"start": v(79.02, 55.85) * mm, "end": v(78.24, 54.52) * mm});
            skLineSegment(sketch, "E13.2.103.0", {"start": v(74.4, 61.88) * mm, "end": v(72.92, 61.46) * mm});
            skLineSegment(sketch, "E13.3.103.0", {"start": v(74.4, 61.88) * mm, "end": v(76, 59.9) * mm});
            skLineSegment(sketch, "E13.6.103.0", {"start": v(76, 59.9) * mm, "end": v(75.28, 58.54) * mm});
            skLineSegment(sketch, "E13.2.104.0", {"start": v(71.06, 65.68) * mm, "end": v(69.6, 65.2) * mm});
            skLineSegment(sketch, "E13.3.104.0", {"start": v(71.06, 65.68) * mm, "end": v(72.75, 63.8) * mm});
            skLineSegment(sketch, "E13.6.104.0", {"start": v(72.75, 63.8) * mm, "end": v(72.11, 62.4) * mm});
            skLineSegment(sketch, "E13.2.105.0", {"start": v(67.52, 69.31) * mm, "end": v(66.1, 68.75) * mm});
            skLineSegment(sketch, "E13.3.105.0", {"start": v(67.52, 69.31) * mm, "end": v(69.31, 67.52) * mm});
            skLineSegment(sketch, "E13.6.105.0", {"start": v(69.31, 67.52) * mm, "end": v(68.75, 66.1) * mm});
            skLineSegment(sketch, "E13.2.106.0", {"start": v(63.8, 72.75) * mm, "end": v(62.4, 72.11) * mm});
            skLineSegment(sketch, "E13.3.106.0", {"start": v(63.8, 72.75) * mm, "end": v(65.68, 71.06) * mm});
            skLineSegment(sketch, "E13.6.106.0", {"start": v(65.68, 71.06) * mm, "end": v(65.2, 69.6) * mm});
            skLineSegment(sketch, "E13.2.107.0", {"start": v(59.9, 76) * mm, "end": v(58.54, 75.28) * mm});
            skLineSegment(sketch, "E13.3.107.0", {"start": v(59.9, 76) * mm, "end": v(61.88, 74.4) * mm});
            skLineSegment(sketch, "E13.6.107.0", {"start": v(61.88, 74.4) * mm, "end": v(61.46, 72.92) * mm});
            skLineSegment(sketch, "E13.2.108.0", {"start": v(55.85, 79.02) * mm, "end": v(54.52, 78.24) * mm});
            skLineSegment(sketch, "E13.3.108.0", {"start": v(55.85, 79.02) * mm, "end": v(57.9, 77.53) * mm});
            skLineSegment(sketch, "E13.6.108.0", {"start": v(57.9, 77.53) * mm, "end": v(57.56, 76.03) * mm});
            skLineSegment(sketch, "E13.2.109.0", {"start": v(51.64, 81.84) * mm, "end": v(50.35, 80.99) * mm});
            skLineSegment(sketch, "E13.3.109.0", {"start": v(51.64, 81.84) * mm, "end": v(53.76, 80.46) * mm});
            skLineSegment(sketch, "E13.6.109.0", {"start": v(53.76, 80.46) * mm, "end": v(53.5, 78.94) * mm});
            skLineSegment(sketch, "E13.2.110.0", {"start": v(47.28, 84.43) * mm, "end": v(46.05, 83.51) * mm});
            skLineSegment(sketch, "E13.3.110.0", {"start": v(47.28, 84.43) * mm, "end": v(49.48, 83.16) * mm});
            skLineSegment(sketch, "E13.6.110.0", {"start": v(49.48, 83.16) * mm, "end": v(49.3, 81.63) * mm});
            skLineSegment(sketch, "E13.2.111.0", {"start": v(42.8, 86.79) * mm, "end": v(41.61, 85.8) * mm});
            skLineSegment(sketch, "E13.3.111.0", {"start": v(42.8, 86.79) * mm, "end": v(45.06, 85.64) * mm});
            skLineSegment(sketch, "E13.6.111.0", {"start": v(45.06, 85.64) * mm, "end": v(44.96, 84.1) * mm});
            skLineSegment(sketch, "E13.2.112.0", {"start": v(38.2, 88.9) * mm, "end": v(37.06, 87.87) * mm});
            skLineSegment(sketch, "E13.3.112.0", {"start": v(38.2, 88.9) * mm, "end": v(40.51, 87.88) * mm});
            skLineSegment(sketch, "E13.6.112.0", {"start": v(40.51, 87.88) * mm, "end": v(40.5, 86.34) * mm});
            skLineSegment(sketch, "E13.2.113.0", {"start": v(33.5, 90.78) * mm, "end": v(32.41, 89.69) * mm});
            skLineSegment(sketch, "E13.3.113.0", {"start": v(33.5, 90.78) * mm, "end": v(35.86, 89.88) * mm});
            skLineSegment(sketch, "E13.6.113.0", {"start": v(35.86, 89.88) * mm, "end": v(35.92, 88.34) * mm});
            skLineSegment(sketch, "E13.2.114.0", {"start": v(28.7, 92.41) * mm, "end": v(27.68, 91.26) * mm});
            skLineSegment(sketch, "E13.3.114.0", {"start": v(28.7, 92.41) * mm, "end": v(31.1, 91.63) * mm});
            skLineSegment(sketch, "E13.6.114.0", {"start": v(31.1, 91.63) * mm, "end": v(31.25, 90.1) * mm});
            skLineSegment(sketch, "E13.2.115.0", {"start": v(23.82, 93.79) * mm, "end": v(22.86, 92.58) * mm});
            skLineSegment(sketch, "E13.3.115.0", {"start": v(23.82, 93.79) * mm, "end": v(26.27, 93.13) * mm});
            skLineSegment(sketch, "E13.6.115.0", {"start": v(26.27, 93.13) * mm, "end": v(26.5, 91.61) * mm});
            skLineSegment(sketch, "E13.2.116.0", {"start": v(18.88, 94.9) * mm, "end": v(17.98, 93.65) * mm});
            skLineSegment(sketch, "E13.3.116.0", {"start": v(18.88, 94.9) * mm, "end": v(21.36, 94.38) * mm});
            skLineSegment(sketch, "E13.6.116.0", {"start": v(21.36, 94.38) * mm, "end": v(21.66, 92.87) * mm});
            skLineSegment(sketch, "E13.2.117.0", {"start": v(13.89, 95.76) * mm, "end": v(13.06, 94.47) * mm});
            skLineSegment(sketch, "E13.3.117.0", {"start": v(13.89, 95.76) * mm, "end": v(16.39, 95.37) * mm});
            skLineSegment(sketch, "E13.6.117.0", {"start": v(16.39, 95.37) * mm, "end": v(16.77, 93.88) * mm});
            skLineSegment(sketch, "E13.2.118.0", {"start": v(8.85, 96.36) * mm, "end": v(8.1, 95.02) * mm});
            skLineSegment(sketch, "E13.3.118.0", {"start": v(8.85, 96.36) * mm, "end": v(11.37, 96.1) * mm});
            skLineSegment(sketch, "E13.6.118.0", {"start": v(11.37, 96.1) * mm, "end": v(11.84, 94.63) * mm});
            skLineSegment(sketch, "E13.2.119.0", {"start": v(3.8, 96.7) * mm, "end": v(3.11, 95.31) * mm});
            skLineSegment(sketch, "E13.3.119.0", {"start": v(3.8, 96.7) * mm, "end": v(6.33, 96.56) * mm});
            skLineSegment(sketch, "E13.6.119.0", {"start": v(6.33, 96.56) * mm, "end": v(6.87, 95.12) * mm});
            skCircle(sketch, "E14", {"center": v(0, 0) * mm, "radius": 4.5 * mm});
            skSolve(sketch);
        }
        {
            var Q0;
            Q0=qSketchRegion(id+"F0",true);
            extrude(context, id + "F1", {"entities" : qUnion([Q0]), "depth" : 15 * mm});
        }
        {
            var Q0;
            Q0=makeQuery(id+"F1.opExtrude","CAP_FACE",FACE,{"disambiguationData":[OSD([sQuery(id+"F0.wireOp",EDGE,"E2"),sQuery(id+"F0.wireOp",EDGE,"E7"),sQuery(id+"F0.wireOp",EDGE,"E8"),sQuery(id+"F0.wireOp",EDGE,"E9.MirrorCS"),sQuery(id+"F0.wireOp",EDGE,"E10.1.0"),sQuery(id+"F0.wireOp",EDGE,"E10.1.1"),sQuery(id+"F0.wireOp",EDGE,"E10.1.2"),sQuery(id+"F0.wireOp",EDGE,"E10.2.0"),sQuery(id+"F0.wireOp",EDGE,"E10.2.1"),sQuery(id+"F0.wireOp",EDGE,"E10.2.2"),sQuery(id+"F0.wireOp",EDGE,"E10.3.0"),sQuery(id+"F0.wireOp",EDGE,"E10.3.1"),sQuery(id+"F0.wireOp",EDGE,"E10.3.2"),sQuery(id+"F0.wireOp",EDGE,"E10.4.0"),sQuery(id+"F0.wireOp",EDGE,"E10.4.1"),sQuery(id+"F0.wireOp",EDGE,"E10.4.2"),sQuery(id+"F0.wireOp",EDGE,"E10.5.0"),sQuery(id+"F0.wireOp",EDGE,"E10.5.1"),sQuery(id+"F0.wireOp",EDGE,"E10.5.2"),sQuery(id+"F0.wireOp",EDGE,"E10.6.0"),sQuery(id+"F0.wireOp",EDGE,"E10.6.1"),sQuery(id+"F0.wireOp",EDGE,"E10.6.2"),sQuery(id+"F0.wireOp",EDGE,"E10.7.0"),sQuery(id+"F0.wireOp",EDGE,"E10.7.1"),sQuery(id+"F0.wireOp",EDGE,"E10.7.2"),sQuery(id+"F0.wireOp",EDGE,"E10.8.0"),sQuery(id+"F0.wireOp",EDGE,"E10.8.1"),sQuery(id+"F0.wireOp",EDGE,"E10.8.2"),sQuery(id+"F0.wireOp",EDGE,"E10.9.0"),sQuery(id+"F0.wireOp",EDGE,"E10.9.1"),sQuery(id+"F0.wireOp",EDGE,"E10.9.2"),sQuery(id+"F0.wireOp",EDGE,"E12.2.10.0"),sQuery(id+"F0.wireOp",EDGE,"E12.3.10.0"),sQuery(id+"F0.wireOp",EDGE,"E12.6.10.0"),sQuery(id+"F0.wireOp",EDGE,"E12.2.11.0"),sQuery(id+"F0.wireOp",EDGE,"E12.3.11.0"),sQuery(id+"F0.wireOp",EDGE,"E12.6.11.0"),sQuery(id+"F0.wireOp",EDGE,"E12.2.12.0"),sQuery(id+"F0.wireOp",EDGE,"E12.3.12.0"),sQuery(id+"F0.wireOp",EDGE,"E12.6.12.0"),sQuery(id+"F0.wireOp",EDGE,"E12.2.13.0"),sQuery(id+"F0.wireOp",EDGE,"E12.3.13.0"),sQuery(id+"F0.wireOp",EDGE,"E12.6.13.0"),sQuery(id+"F0.wireOp",EDGE,"E12.2.14.0"),sQuery(id+"F0.wireOp",EDGE,"E12.3.14.0"),sQuery(id+"F0.wireOp",EDGE,"E12.6.14.0"),sQuery(id+"F0.wireOp",EDGE,"E12.2.15.0"),sQuery(id+"F0.wireOp",EDGE,"E12.3.15.0"),sQuery(id+"F0.wireOp",EDGE,"E12.6.15.0"),sQuery(id+"F0.wireOp",EDGE,"E12.2.16.0"),sQuery(id+"F0.wireOp",EDGE,"E12.3.16.0"),sQuery(id+"F0.wireOp",EDGE,"E12.6.16.0"),sQuery(id+"F0.wireOp",EDGE,"E12.2.17.0"),sQuery(id+"F0.wireOp",EDGE,"E12.3.17.0"),sQuery(id+"F0.wireOp",EDGE,"E12.6.17.0"),sQuery(id+"F0.wireOp",EDGE,"E12.2.18.0"),sQuery(id+"F0.wireOp",EDGE,"E12.3.18.0"),sQuery(id+"F0.wireOp",EDGE,"E12.6.18.0"),sQuery(id+"F0.wireOp",EDGE,"E12.2.19.0"),sQuery(id+"F0.wireOp",EDGE,"E12.3.19.0"),sQuery(id+"F0.wireOp",EDGE,"E12.6.19.0"),sQuery(id+"F0.wireOp",EDGE,"E12.2.20.0"),sQuery(id+"F0.wireOp",EDGE,"E12.3.20.0"),sQuery(id+"F0.wireOp",EDGE,"E12.6.20.0"),sQuery(id+"F0.wireOp",EDGE,"E12.2.21.0"),sQuery(id+"F0.wireOp",EDGE,"E12.3.21.0"),sQuery(id+"F0.wireOp",EDGE,"E12.6.21.0"),sQuery(id+"F0.wireOp",EDGE,"E12.2.22.0"),sQuery(id+"F0.wireOp",EDGE,"E12.3.22.0"),sQuery(id+"F0.wireOp",EDGE,"E12.6.22.0"),sQuery(id+"F0.wireOp",EDGE,"E12.2.23.0"),sQuery(id+"F0.wireOp",EDGE,"E12.3.23.0"),sQuery(id+"F0.wireOp",EDGE,"E12.6.23.0"),sQuery(id+"F0.wireOp",EDGE,"E12.2.24.0"),sQuery(id+"F0.wireOp",EDGE,"E12.3.24.0"),sQuery(id+"F0.wireOp",EDGE,"E12.6.24.0"),sQuery(id+"F0.wireOp",EDGE,"E12.2.25.0"),sQuery(id+"F0.wireOp",EDGE,"E12.3.25.0"),sQuery(id+"F0.wireOp",EDGE,"E12.6.25.0"),sQuery(id+"F0.wireOp",EDGE,"E12.2.26.0"),sQuery(id+"F0.wireOp",EDGE,"E12.3.26.0"),sQuery(id+"F0.wireOp",EDGE,"E12.6.26.0"),sQuery(id+"F0.wireOp",EDGE,"E12.2.27.0"),sQuery(id+"F0.wireOp",EDGE,"E12.3.27.0"),sQuery(id+"F0.wireOp",EDGE,"E12.6.27.0"),sQuery(id+"F0.wireOp",EDGE,"E12.2.28.0"),sQuery(id+"F0.wireOp",EDGE,"E12.3.28.0"),sQuery(id+"F0.wireOp",EDGE,"E12.6.28.0"),sQuery(id+"F0.wireOp",EDGE,"E12.2.29.0"),sQuery(id+"F0.wireOp",EDGE,"E12.3.29.0"),sQuery(id+"F0.wireOp",EDGE,"E12.6.29.0"),sQuery(id+"F0.wireOp",EDGE,"E12.2.30.0"),sQuery(id+"F0.wireOp",EDGE,"E12.3.30.0"),sQuery(id+"F0.wireOp",EDGE,"E12.6.30.0"),sQuery(id+"F0.wireOp",EDGE,"E12.2.31.0"),sQuery(id+"F0.wireOp",EDGE,"E12.3.31.0"),sQuery(id+"F0.wireOp",EDGE,"E12.6.31.0"),sQuery(id+"F0.wireOp",EDGE,"E12.2.32.0"),sQuery(id+"F0.wireOp",EDGE,"E12.3.32.0"),sQuery(id+"F0.wireOp",EDGE,"E12.6.32.0"),sQuery(id+"F0.wireOp",EDGE,"E12.2.33.0"),sQuery(id+"F0.wireOp",EDGE,"E12.3.33.0"),sQuery(id+"F0.wireOp",EDGE,"E12.6.33.0"),sQuery(id+"F0.wireOp",EDGE,"E12.2.34.0"),sQuery(id+"F0.wireOp",EDGE,"E12.3.34.0"),sQuery(id+"F0.wireOp",EDGE,"E12.6.34.0"),sQuery(id+"F0.wireOp",EDGE,"E12.2.35.0"),sQuery(id+"F0.wireOp",EDGE,"E12.3.35.0"),sQuery(id+"F0.wireOp",EDGE,"E12.6.35.0"),sQuery(id+"F0.wireOp",EDGE,"E12.2.36.0"),sQuery(id+"F0.wireOp",EDGE,"E12.3.36.0"),sQuery(id+"F0.wireOp",EDGE,"E12.6.36.0"),sQuery(id+"F0.wireOp",EDGE,"E12.2.37.0"),sQuery(id+"F0.wireOp",EDGE,"E12.3.37.0"),sQuery(id+"F0.wireOp",EDGE,"E12.6.37.0"),sQuery(id+"F0.wireOp",EDGE,"E12.2.38.0"),sQuery(id+"F0.wireOp",EDGE,"E12.3.38.0"),sQuery(id+"F0.wireOp",EDGE,"E12.6.38.0"),sQuery(id+"F0.wireOp",EDGE,"E12.2.39.0"),sQuery(id+"F0.wireOp",EDGE,"E12.3.39.0"),sQuery(id+"F0.wireOp",EDGE,"E12.6.39.0"),sQuery(id+"F0.wireOp",EDGE,"E12.2.40.0"),sQuery(id+"F0.wireOp",EDGE,"E12.3.40.0"),sQuery(id+"F0.wireOp",EDGE,"E12.6.40.0"),sQuery(id+"F0.wireOp",EDGE,"E12.2.41.0"),sQuery(id+"F0.wireOp",EDGE,"E12.3.41.0"),sQuery(id+"F0.wireOp",EDGE,"E12.6.41.0"),sQuery(id+"F0.wireOp",EDGE,"E12.2.42.0"),sQuery(id+"F0.wireOp",EDGE,"E12.3.42.0"),sQuery(id+"F0.wireOp",EDGE,"E12.6.42.0"),sQuery(id+"F0.wireOp",EDGE,"E12.2.43.0"),sQuery(id+"F0.wireOp",EDGE,"E12.3.43.0"),sQuery(id+"F0.wireOp",EDGE,"E12.6.43.0"),sQuery(id+"F0.wireOp",EDGE,"E12.2.44.0"),sQuery(id+"F0.wireOp",EDGE,"E12.3.44.0"),sQuery(id+"F0.wireOp",EDGE,"E12.6.44.0"),sQuery(id+"F0.wireOp",EDGE,"E12.2.45.0"),sQuery(id+"F0.wireOp",EDGE,"E12.3.45.0"),sQuery(id+"F0.wireOp",EDGE,"E12.6.45.0"),sQuery(id+"F0.wireOp",EDGE,"E12.2.46.0"),sQuery(id+"F0.wireOp",EDGE,"E12.3.46.0"),sQuery(id+"F0.wireOp",EDGE,"E12.6.46.0"),sQuery(id+"F0.wireOp",EDGE,"E12.2.47.0"),sQuery(id+"F0.wireOp",EDGE,"E12.3.47.0"),sQuery(id+"F0.wireOp",EDGE,"E12.6.47.0"),sQuery(id+"F0.wireOp",EDGE,"E12.2.48.0"),sQuery(id+"F0.wireOp",EDGE,"E12.3.48.0"),sQuery(id+"F0.wireOp",EDGE,"E12.6.48.0"),sQuery(id+"F0.wireOp",EDGE,"E12.2.49.0"),sQuery(id+"F0.wireOp",EDGE,"E12.3.49.0"),sQuery(id+"F0.wireOp",EDGE,"E12.6.49.0"),sQuery(id+"F0.wireOp",EDGE,"E12.2.50.0"),sQuery(id+"F0.wireOp",EDGE,"E12.3.50.0"),sQuery(id+"F0.wireOp",EDGE,"E12.6.50.0"),sQuery(id+"F0.wireOp",EDGE,"E12.2.51.0"),sQuery(id+"F0.wireOp",EDGE,"E12.3.51.0"),sQuery(id+"F0.wireOp",EDGE,"E12.6.51.0"),sQuery(id+"F0.wireOp",EDGE,"E12.2.52.0"),sQuery(id+"F0.wireOp",EDGE,"E12.3.52.0"),sQuery(id+"F0.wireOp",EDGE,"E12.6.52.0"),sQuery(id+"F0.wireOp",EDGE,"E12.2.53.0"),sQuery(id+"F0.wireOp",EDGE,"E12.3.53.0"),sQuery(id+"F0.wireOp",EDGE,"E12.6.53.0"),sQuery(id+"F0.wireOp",EDGE,"E12.2.54.0"),sQuery(id+"F0.wireOp",EDGE,"E12.3.54.0"),sQuery(id+"F0.wireOp",EDGE,"E12.6.54.0"),sQuery(id+"F0.wireOp",EDGE,"E12.2.55.0"),sQuery(id+"F0.wireOp",EDGE,"E12.3.55.0"),sQuery(id+"F0.wireOp",EDGE,"E12.6.55.0"),sQuery(id+"F0.wireOp",EDGE,"E12.2.56.0"),sQuery(id+"F0.wireOp",EDGE,"E12.3.56.0"),sQuery(id+"F0.wireOp",EDGE,"E12.6.56.0"),sQuery(id+"F0.wireOp",EDGE,"E12.2.57.0"),sQuery(id+"F0.wireOp",EDGE,"E12.3.57.0"),sQuery(id+"F0.wireOp",EDGE,"E12.6.57.0"),sQuery(id+"F0.wireOp",EDGE,"E12.2.58.0"),sQuery(id+"F0.wireOp",EDGE,"E12.3.58.0"),sQuery(id+"F0.wireOp",EDGE,"E12.6.58.0"),sQuery(id+"F0.wireOp",EDGE,"E12.2.59.0"),sQuery(id+"F0.wireOp",EDGE,"E12.3.59.0"),sQuery(id+"F0.wireOp",EDGE,"E12.6.59.0"),sQuery(id+"F0.wireOp",EDGE,"E13.2.60.0"),sQuery(id+"F0.wireOp",EDGE,"E13.3.60.0"),sQuery(id+"F0.wireOp",EDGE,"E13.6.60.0"),sQuery(id+"F0.wireOp",EDGE,"E13.2.61.0"),sQuery(id+"F0.wireOp",EDGE,"E13.3.61.0"),sQuery(id+"F0.wireOp",EDGE,"E13.6.61.0"),sQuery(id+"F0.wireOp",EDGE,"E13.2.62.0"),sQuery(id+"F0.wireOp",EDGE,"E13.3.62.0"),sQuery(id+"F0.wireOp",EDGE,"E13.6.62.0"),sQuery(id+"F0.wireOp",EDGE,"E13.2.63.0"),sQuery(id+"F0.wireOp",EDGE,"E13.3.63.0"),sQuery(id+"F0.wireOp",EDGE,"E13.6.63.0"),sQuery(id+"F0.wireOp",EDGE,"E13.2.64.0"),sQuery(id+"F0.wireOp",EDGE,"E13.3.64.0"),sQuery(id+"F0.wireOp",EDGE,"E13.6.64.0"),sQuery(id+"F0.wireOp",EDGE,"E13.2.65.0"),sQuery(id+"F0.wireOp",EDGE,"E13.3.65.0"),sQuery(id+"F0.wireOp",EDGE,"E13.6.65.0"),sQuery(id+"F0.wireOp",EDGE,"E13.2.66.0"),sQuery(id+"F0.wireOp",EDGE,"E13.3.66.0"),sQuery(id+"F0.wireOp",EDGE,"E13.6.66.0"),sQuery(id+"F0.wireOp",EDGE,"E13.2.67.0"),sQuery(id+"F0.wireOp",EDGE,"E13.3.67.0"),sQuery(id+"F0.wireOp",EDGE,"E13.6.67.0"),sQuery(id+"F0.wireOp",EDGE,"E13.2.68.0"),sQuery(id+"F0.wireOp",EDGE,"E13.3.68.0"),sQuery(id+"F0.wireOp",EDGE,"E13.6.68.0"),sQuery(id+"F0.wireOp",EDGE,"E13.2.69.0"),sQuery(id+"F0.wireOp",EDGE,"E13.3.69.0"),sQuery(id+"F0.wireOp",EDGE,"E13.6.69.0"),sQuery(id+"F0.wireOp",EDGE,"E13.2.70.0"),sQuery(id+"F0.wireOp",EDGE,"E13.3.70.0"),sQuery(id+"F0.wireOp",EDGE,"E13.6.70.0"),sQuery(id+"F0.wireOp",EDGE,"E13.2.71.0"),sQuery(id+"F0.wireOp",EDGE,"E13.3.71.0"),sQuery(id+"F0.wireOp",EDGE,"E13.6.71.0"),sQuery(id+"F0.wireOp",EDGE,"E13.2.72.0"),sQuery(id+"F0.wireOp",EDGE,"E13.3.72.0"),sQuery(id+"F0.wireOp",EDGE,"E13.6.72.0"),sQuery(id+"F0.wireOp",EDGE,"E13.2.73.0"),sQuery(id+"F0.wireOp",EDGE,"E13.3.73.0"),sQuery(id+"F0.wireOp",EDGE,"E13.6.73.0"),sQuery(id+"F0.wireOp",EDGE,"E13.2.74.0"),sQuery(id+"F0.wireOp",EDGE,"E13.3.74.0"),sQuery(id+"F0.wireOp",EDGE,"E13.6.74.0"),sQuery(id+"F0.wireOp",EDGE,"E13.2.75.0"),sQuery(id+"F0.wireOp",EDGE,"E13.3.75.0"),sQuery(id+"F0.wireOp",EDGE,"E13.6.75.0"),sQuery(id+"F0.wireOp",EDGE,"E13.2.76.0"),sQuery(id+"F0.wireOp",EDGE,"E13.3.76.0"),sQuery(id+"F0.wireOp",EDGE,"E13.6.76.0"),sQuery(id+"F0.wireOp",EDGE,"E13.2.77.0"),sQuery(id+"F0.wireOp",EDGE,"E13.3.77.0"),sQuery(id+"F0.wireOp",EDGE,"E13.6.77.0"),sQuery(id+"F0.wireOp",EDGE,"E13.2.78.0"),sQuery(id+"F0.wireOp",EDGE,"E13.3.78.0"),sQuery(id+"F0.wireOp",EDGE,"E13.6.78.0"),sQuery(id+"F0.wireOp",EDGE,"E13.2.79.0"),sQuery(id+"F0.wireOp",EDGE,"E13.3.79.0"),sQuery(id+"F0.wireOp",EDGE,"E13.6.79.0"),sQuery(id+"F0.wireOp",EDGE,"E13.2.80.0"),sQuery(id+"F0.wireOp",EDGE,"E13.3.80.0"),sQuery(id+"F0.wireOp",EDGE,"E13.6.80.0"),sQuery(id+"F0.wireOp",EDGE,"E13.2.81.0"),sQuery(id+"F0.wireOp",EDGE,"E13.3.81.0"),sQuery(id+"F0.wireOp",EDGE,"E13.6.81.0"),sQuery(id+"F0.wireOp",EDGE,"E13.2.82.0"),sQuery(id+"F0.wireOp",EDGE,"E13.3.82.0"),sQuery(id+"F0.wireOp",EDGE,"E13.6.82.0"),sQuery(id+"F0.wireOp",EDGE,"E13.2.83.0"),sQuery(id+"F0.wireOp",EDGE,"E13.3.83.0"),sQuery(id+"F0.wireOp",EDGE,"E13.6.83.0"),sQuery(id+"F0.wireOp",EDGE,"E13.2.84.0"),sQuery(id+"F0.wireOp",EDGE,"E13.3.84.0"),sQuery(id+"F0.wireOp",EDGE,"E13.6.84.0"),sQuery(id+"F0.wireOp",EDGE,"E13.2.85.0"),sQuery(id+"F0.wireOp",EDGE,"E13.3.85.0"),sQuery(id+"F0.wireOp",EDGE,"E13.6.85.0"),sQuery(id+"F0.wireOp",EDGE,"E13.2.86.0"),sQuery(id+"F0.wireOp",EDGE,"E13.3.86.0"),sQuery(id+"F0.wireOp",EDGE,"E13.6.86.0"),sQuery(id+"F0.wireOp",EDGE,"E13.2.87.0"),sQuery(id+"F0.wireOp",EDGE,"E13.3.87.0"),sQuery(id+"F0.wireOp",EDGE,"E13.6.87.0"),sQuery(id+"F0.wireOp",EDGE,"E13.2.88.0"),sQuery(id+"F0.wireOp",EDGE,"E13.3.88.0"),sQuery(id+"F0.wireOp",EDGE,"E13.6.88.0"),sQuery(id+"F0.wireOp",EDGE,"E13.2.89.0"),sQuery(id+"F0.wireOp",EDGE,"E13.3.89.0"),sQuery(id+"F0.wireOp",EDGE,"E13.6.89.0"),sQuery(id+"F0.wireOp",EDGE,"E13.2.90.0"),sQuery(id+"F0.wireOp",EDGE,"E13.3.90.0"),sQuery(id+"F0.wireOp",EDGE,"E13.6.90.0"),sQuery(id+"F0.wireOp",EDGE,"E13.2.91.0"),sQuery(id+"F0.wireOp",EDGE,"E13.3.91.0"),sQuery(id+"F0.wireOp",EDGE,"E13.6.91.0"),sQuery(id+"F0.wireOp",EDGE,"E13.2.92.0"),sQuery(id+"F0.wireOp",EDGE,"E13.3.92.0"),sQuery(id+"F0.wireOp",EDGE,"E13.6.92.0"),sQuery(id+"F0.wireOp",EDGE,"E13.2.93.0"),sQuery(id+"F0.wireOp",EDGE,"E13.3.93.0"),sQuery(id+"F0.wireOp",EDGE,"E13.6.93.0"),sQuery(id+"F0.wireOp",EDGE,"E13.2.94.0"),sQuery(id+"F0.wireOp",EDGE,"E13.3.94.0"),sQuery(id+"F0.wireOp",EDGE,"E13.6.94.0"),sQuery(id+"F0.wireOp",EDGE,"E13.2.95.0"),sQuery(id+"F0.wireOp",EDGE,"E13.3.95.0"),sQuery(id+"F0.wireOp",EDGE,"E13.6.95.0"),sQuery(id+"F0.wireOp",EDGE,"E13.2.96.0"),sQuery(id+"F0.wireOp",EDGE,"E13.3.96.0"),sQuery(id+"F0.wireOp",EDGE,"E13.6.96.0"),sQuery(id+"F0.wireOp",EDGE,"E13.2.97.0"),sQuery(id+"F0.wireOp",EDGE,"E13.3.97.0"),sQuery(id+"F0.wireOp",EDGE,"E13.6.97.0"),sQuery(id+"F0.wireOp",EDGE,"E13.2.98.0"),sQuery(id+"F0.wireOp",EDGE,"E13.3.98.0"),sQuery(id+"F0.wireOp",EDGE,"E13.6.98.0"),sQuery(id+"F0.wireOp",EDGE,"E13.2.99.0"),sQuery(id+"F0.wireOp",EDGE,"E13.3.99.0"),sQuery(id+"F0.wireOp",EDGE,"E13.6.99.0"),sQuery(id+"F0.wireOp",EDGE,"E13.2.100.0"),sQuery(id+"F0.wireOp",EDGE,"E13.3.100.0"),sQuery(id+"F0.wireOp",EDGE,"E13.6.100.0"),sQuery(id+"F0.wireOp",EDGE,"E13.2.101.0"),sQuery(id+"F0.wireOp",EDGE,"E13.3.101.0"),sQuery(id+"F0.wireOp",EDGE,"E13.6.101.0"),sQuery(id+"F0.wireOp",EDGE,"E13.2.102.0"),sQuery(id+"F0.wireOp",EDGE,"E13.3.102.0"),sQuery(id+"F0.wireOp",EDGE,"E13.6.102.0"),sQuery(id+"F0.wireOp",EDGE,"E13.2.103.0"),sQuery(id+"F0.wireOp",EDGE,"E13.3.103.0"),sQuery(id+"F0.wireOp",EDGE,"E13.6.103.0"),sQuery(id+"F0.wireOp",EDGE,"E13.2.104.0"),sQuery(id+"F0.wireOp",EDGE,"E13.3.104.0"),sQuery(id+"F0.wireOp",EDGE,"E13.6.104.0"),sQuery(id+"F0.wireOp",EDGE,"E13.2.105.0"),sQuery(id+"F0.wireOp",EDGE,"E13.3.105.0"),sQuery(id+"F0.wireOp",EDGE,"E13.6.105.0"),sQuery(id+"F0.wireOp",EDGE,"E13.2.106.0"),sQuery(id+"F0.wireOp",EDGE,"E13.3.106.0"),sQuery(id+"F0.wireOp",EDGE,"E13.6.106.0"),sQuery(id+"F0.wireOp",EDGE,"E13.2.107.0"),sQuery(id+"F0.wireOp",EDGE,"E13.3.107.0"),sQuery(id+"F0.wireOp",EDGE,"E13.6.107.0"),sQuery(id+"F0.wireOp",EDGE,"E13.2.108.0"),sQuery(id+"F0.wireOp",EDGE,"E13.3.108.0"),sQuery(id+"F0.wireOp",EDGE,"E13.6.108.0"),sQuery(id+"F0.wireOp",EDGE,"E13.2.109.0"),sQuery(id+"F0.wireOp",EDGE,"E13.3.109.0"),sQuery(id+"F0.wireOp",EDGE,"E13.6.109.0"),sQuery(id+"F0.wireOp",EDGE,"E13.2.110.0"),sQuery(id+"F0.wireOp",EDGE,"E13.3.110.0"),sQuery(id+"F0.wireOp",EDGE,"E13.6.110.0"),sQuery(id+"F0.wireOp",EDGE,"E13.2.111.0"),sQuery(id+"F0.wireOp",EDGE,"E13.3.111.0"),sQuery(id+"F0.wireOp",EDGE,"E13.6.111.0"),sQuery(id+"F0.wireOp",EDGE,"E13.2.112.0"),sQuery(id+"F0.wireOp",EDGE,"E13.3.112.0"),sQuery(id+"F0.wireOp",EDGE,"E13.6.112.0"),sQuery(id+"F0.wireOp",EDGE,"E13.2.113.0"),sQuery(id+"F0.wireOp",EDGE,"E13.3.113.0"),sQuery(id+"F0.wireOp",EDGE,"E13.6.113.0"),sQuery(id+"F0.wireOp",EDGE,"E13.2.114.0"),sQuery(id+"F0.wireOp",EDGE,"E13.3.114.0"),sQuery(id+"F0.wireOp",EDGE,"E13.6.114.0"),sQuery(id+"F0.wireOp",EDGE,"E13.2.115.0"),sQuery(id+"F0.wireOp",EDGE,"E13.3.115.0"),sQuery(id+"F0.wireOp",EDGE,"E13.6.115.0"),sQuery(id+"F0.wireOp",EDGE,"E13.2.116.0"),sQuery(id+"F0.wireOp",EDGE,"E13.3.116.0"),sQuery(id+"F0.wireOp",EDGE,"E13.6.116.0"),sQuery(id+"F0.wireOp",EDGE,"E13.2.117.0"),sQuery(id+"F0.wireOp",EDGE,"E13.3.117.0"),sQuery(id+"F0.wireOp",EDGE,"E13.6.117.0"),sQuery(id+"F0.wireOp",EDGE,"E13.2.118.0"),sQuery(id+"F0.wireOp",EDGE,"E13.3.118.0"),sQuery(id+"F0.wireOp",EDGE,"E13.6.118.0"),sQuery(id+"F0.wireOp",EDGE,"E13.2.119.0"),sQuery(id+"F0.wireOp",EDGE,"E13.3.119.0"),sQuery(id+"F0.wireOp",EDGE,"E13.6.119.0"),sQuery(id+"F0.wireOp",EDGE,"E14")])],"isStart":false});
            var sketch = newSketch(context, id + "F2", { "sketchPlane" : qUnion([Q0])});
            skLineSegment(sketch, "E15.bottom", {"start": v(-55, 55) * mm, "end": v(55, 55) * mm, "construction": true});
            skLineSegment(sketch, "E15.top", {"start": v(-55, -55) * mm, "end": v(55, -55) * mm, "construction": true});
            skLineSegment(sketch, "E15.left", {"start": v(-55, 55) * mm, "end": v(-55, -55) * mm, "construction": true});
            skLineSegment(sketch, "E15.right", {"start": v(55, 55) * mm, "end": v(55, -55) * mm, "construction": true});
            skPoint(sketch, "E15.middle", {"position": v(0, 0) * mm});
            skCircle(sketch, "E16", {"center": v(-55, 55) * mm, "radius": 1.5 * mm});
            skCircle(sketch, "E17", {"center": v(55, 55) * mm, "radius": 1.5 * mm});
            skCircle(sketch, "E18", {"center": v(-55, -55) * mm, "radius": 1.5 * mm});
            skCircle(sketch, "E19", {"center": v(55, -55) * mm, "radius": 1.5 * mm});
            skLineSegment(sketch, "E20.bottom", {"start": v(45, 45) * mm, "end": v(-45, 45) * mm, "construction": true});
            skLineSegment(sketch, "E20.top", {"start": v(45, -45) * mm, "end": v(-45, -45) * mm, "construction": true});
            skLineSegment(sketch, "E20.left", {"start": v(45, 45) * mm, "end": v(45, -45) * mm, "construction": true});
            skLineSegment(sketch, "E20.right", {"start": v(-45, 45) * mm, "end": v(-45, -45) * mm, "construction": true});
            skCircle(sketch, "E21", {"center": v(-45, 45) * mm, "radius": 1.5 * mm});
            skCircle(sketch, "E22.MirrorC", {"center": v(45, 45) * mm, "radius": 1.5 * mm});
            skCircle(sketch, "E23.MirrorC", {"center": v(-45, -45) * mm, "radius": 1.5 * mm});
            skCircle(sketch, "E24.MirrorC", {"center": v(45, -45) * mm, "radius": 1.5 * mm});
            skSolve(sketch);
        }
        {
            var Q0;
            Q0 = qSketchRegion(id + "F2", true);
            var Q1;
            Q1=makeQuery(id+"F1.opExtrude","CAP_FACE",FACE,{"disambiguationData":[OSD([sQuery(id+"F0.wireOp",EDGE,"E2"),sQuery(id+"F0.wireOp",EDGE,"E7"),sQuery(id+"F0.wireOp",EDGE,"E8"),sQuery(id+"F0.wireOp",EDGE,"E9.MirrorCS"),sQuery(id+"F0.wireOp",EDGE,"E10.1.0"),sQuery(id+"F0.wireOp",EDGE,"E10.1.1"),sQuery(id+"F0.wireOp",EDGE,"E10.1.2"),sQuery(id+"F0.wireOp",EDGE,"E10.2.0"),sQuery(id+"F0.wireOp",EDGE,"E10.2.1"),sQuery(id+"F0.wireOp",EDGE,"E10.2.2"),sQuery(id+"F0.wireOp",EDGE,"E10.3.0"),sQuery(id+"F0.wireOp",EDGE,"E10.3.1"),sQuery(id+"F0.wireOp",EDGE,"E10.3.2"),sQuery(id+"F0.wireOp",EDGE,"E10.4.0"),sQuery(id+"F0.wireOp",EDGE,"E10.4.1"),sQuery(id+"F0.wireOp",EDGE,"E10.4.2"),sQuery(id+"F0.wireOp",EDGE,"E10.5.0"),sQuery(id+"F0.wireOp",EDGE,"E10.5.1"),sQuery(id+"F0.wireOp",EDGE,"E10.5.2"),sQuery(id+"F0.wireOp",EDGE,"E10.6.0"),sQuery(id+"F0.wireOp",EDGE,"E10.6.1"),sQuery(id+"F0.wireOp",EDGE,"E10.6.2"),sQuery(id+"F0.wireOp",EDGE,"E10.7.0"),sQuery(id+"F0.wireOp",EDGE,"E10.7.1"),sQuery(id+"F0.wireOp",EDGE,"E10.7.2"),sQuery(id+"F0.wireOp",EDGE,"E10.8.0"),sQuery(id+"F0.wireOp",EDGE,"E10.8.1"),sQuery(id+"F0.wireOp",EDGE,"E10.8.2"),sQuery(id+"F0.wireOp",EDGE,"E10.9.0"),sQuery(id+"F0.wireOp",EDGE,"E10.9.1"),sQuery(id+"F0.wireOp",EDGE,"E10.9.2"),sQuery(id+"F0.wireOp",EDGE,"E12.2.10.0"),sQuery(id+"F0.wireOp",EDGE,"E12.3.10.0"),sQuery(id+"F0.wireOp",EDGE,"E12.6.10.0"),sQuery(id+"F0.wireOp",EDGE,"E12.2.11.0"),sQuery(id+"F0.wireOp",EDGE,"E12.3.11.0"),sQuery(id+"F0.wireOp",EDGE,"E12.6.11.0"),sQuery(id+"F0.wireOp",EDGE,"E12.2.12.0"),sQuery(id+"F0.wireOp",EDGE,"E12.3.12.0"),sQuery(id+"F0.wireOp",EDGE,"E12.6.12.0"),sQuery(id+"F0.wireOp",EDGE,"E12.2.13.0"),sQuery(id+"F0.wireOp",EDGE,"E12.3.13.0"),sQuery(id+"F0.wireOp",EDGE,"E12.6.13.0"),sQuery(id+"F0.wireOp",EDGE,"E12.2.14.0"),sQuery(id+"F0.wireOp",EDGE,"E12.3.14.0"),sQuery(id+"F0.wireOp",EDGE,"E12.6.14.0"),sQuery(id+"F0.wireOp",EDGE,"E12.2.15.0"),sQuery(id+"F0.wireOp",EDGE,"E12.3.15.0"),sQuery(id+"F0.wireOp",EDGE,"E12.6.15.0"),sQuery(id+"F0.wireOp",EDGE,"E12.2.16.0"),sQuery(id+"F0.wireOp",EDGE,"E12.3.16.0"),sQuery(id+"F0.wireOp",EDGE,"E12.6.16.0"),sQuery(id+"F0.wireOp",EDGE,"E12.2.17.0"),sQuery(id+"F0.wireOp",EDGE,"E12.3.17.0"),sQuery(id+"F0.wireOp",EDGE,"E12.6.17.0"),sQuery(id+"F0.wireOp",EDGE,"E12.2.18.0"),sQuery(id+"F0.wireOp",EDGE,"E12.3.18.0"),sQuery(id+"F0.wireOp",EDGE,"E12.6.18.0"),sQuery(id+"F0.wireOp",EDGE,"E12.2.19.0"),sQuery(id+"F0.wireOp",EDGE,"E12.3.19.0"),sQuery(id+"F0.wireOp",EDGE,"E12.6.19.0"),sQuery(id+"F0.wireOp",EDGE,"E12.2.20.0"),sQuery(id+"F0.wireOp",EDGE,"E12.3.20.0"),sQuery(id+"F0.wireOp",EDGE,"E12.6.20.0"),sQuery(id+"F0.wireOp",EDGE,"E12.2.21.0"),sQuery(id+"F0.wireOp",EDGE,"E12.3.21.0"),sQuery(id+"F0.wireOp",EDGE,"E12.6.21.0"),sQuery(id+"F0.wireOp",EDGE,"E12.2.22.0"),sQuery(id+"F0.wireOp",EDGE,"E12.3.22.0"),sQuery(id+"F0.wireOp",EDGE,"E12.6.22.0"),sQuery(id+"F0.wireOp",EDGE,"E12.2.23.0"),sQuery(id+"F0.wireOp",EDGE,"E12.3.23.0"),sQuery(id+"F0.wireOp",EDGE,"E12.6.23.0"),sQuery(id+"F0.wireOp",EDGE,"E12.2.24.0"),sQuery(id+"F0.wireOp",EDGE,"E12.3.24.0"),sQuery(id+"F0.wireOp",EDGE,"E12.6.24.0"),sQuery(id+"F0.wireOp",EDGE,"E12.2.25.0"),sQuery(id+"F0.wireOp",EDGE,"E12.3.25.0"),sQuery(id+"F0.wireOp",EDGE,"E12.6.25.0"),sQuery(id+"F0.wireOp",EDGE,"E12.2.26.0"),sQuery(id+"F0.wireOp",EDGE,"E12.3.26.0"),sQuery(id+"F0.wireOp",EDGE,"E12.6.26.0"),sQuery(id+"F0.wireOp",EDGE,"E12.2.27.0"),sQuery(id+"F0.wireOp",EDGE,"E12.3.27.0"),sQuery(id+"F0.wireOp",EDGE,"E12.6.27.0"),sQuery(id+"F0.wireOp",EDGE,"E12.2.28.0"),sQuery(id+"F0.wireOp",EDGE,"E12.3.28.0"),sQuery(id+"F0.wireOp",EDGE,"E12.6.28.0"),sQuery(id+"F0.wireOp",EDGE,"E12.2.29.0"),sQuery(id+"F0.wireOp",EDGE,"E12.3.29.0"),sQuery(id+"F0.wireOp",EDGE,"E12.6.29.0"),sQuery(id+"F0.wireOp",EDGE,"E12.2.30.0"),sQuery(id+"F0.wireOp",EDGE,"E12.3.30.0"),sQuery(id+"F0.wireOp",EDGE,"E12.6.30.0"),sQuery(id+"F0.wireOp",EDGE,"E12.2.31.0"),sQuery(id+"F0.wireOp",EDGE,"E12.3.31.0"),sQuery(id+"F0.wireOp",EDGE,"E12.6.31.0"),sQuery(id+"F0.wireOp",EDGE,"E12.2.32.0"),sQuery(id+"F0.wireOp",EDGE,"E12.3.32.0"),sQuery(id+"F0.wireOp",EDGE,"E12.6.32.0"),sQuery(id+"F0.wireOp",EDGE,"E12.2.33.0"),sQuery(id+"F0.wireOp",EDGE,"E12.3.33.0"),sQuery(id+"F0.wireOp",EDGE,"E12.6.33.0"),sQuery(id+"F0.wireOp",EDGE,"E12.2.34.0"),sQuery(id+"F0.wireOp",EDGE,"E12.3.34.0"),sQuery(id+"F0.wireOp",EDGE,"E12.6.34.0"),sQuery(id+"F0.wireOp",EDGE,"E12.2.35.0"),sQuery(id+"F0.wireOp",EDGE,"E12.3.35.0"),sQuery(id+"F0.wireOp",EDGE,"E12.6.35.0"),sQuery(id+"F0.wireOp",EDGE,"E12.2.36.0"),sQuery(id+"F0.wireOp",EDGE,"E12.3.36.0"),sQuery(id+"F0.wireOp",EDGE,"E12.6.36.0"),sQuery(id+"F0.wireOp",EDGE,"E12.2.37.0"),sQuery(id+"F0.wireOp",EDGE,"E12.3.37.0"),sQuery(id+"F0.wireOp",EDGE,"E12.6.37.0"),sQuery(id+"F0.wireOp",EDGE,"E12.2.38.0"),sQuery(id+"F0.wireOp",EDGE,"E12.3.38.0"),sQuery(id+"F0.wireOp",EDGE,"E12.6.38.0"),sQuery(id+"F0.wireOp",EDGE,"E12.2.39.0"),sQuery(id+"F0.wireOp",EDGE,"E12.3.39.0"),sQuery(id+"F0.wireOp",EDGE,"E12.6.39.0"),sQuery(id+"F0.wireOp",EDGE,"E12.2.40.0"),sQuery(id+"F0.wireOp",EDGE,"E12.3.40.0"),sQuery(id+"F0.wireOp",EDGE,"E12.6.40.0"),sQuery(id+"F0.wireOp",EDGE,"E12.2.41.0"),sQuery(id+"F0.wireOp",EDGE,"E12.3.41.0"),sQuery(id+"F0.wireOp",EDGE,"E12.6.41.0"),sQuery(id+"F0.wireOp",EDGE,"E12.2.42.0"),sQuery(id+"F0.wireOp",EDGE,"E12.3.42.0"),sQuery(id+"F0.wireOp",EDGE,"E12.6.42.0"),sQuery(id+"F0.wireOp",EDGE,"E12.2.43.0"),sQuery(id+"F0.wireOp",EDGE,"E12.3.43.0"),sQuery(id+"F0.wireOp",EDGE,"E12.6.43.0"),sQuery(id+"F0.wireOp",EDGE,"E12.2.44.0"),sQuery(id+"F0.wireOp",EDGE,"E12.3.44.0"),sQuery(id+"F0.wireOp",EDGE,"E12.6.44.0"),sQuery(id+"F0.wireOp",EDGE,"E12.2.45.0"),sQuery(id+"F0.wireOp",EDGE,"E12.3.45.0"),sQuery(id+"F0.wireOp",EDGE,"E12.6.45.0"),sQuery(id+"F0.wireOp",EDGE,"E12.2.46.0"),sQuery(id+"F0.wireOp",EDGE,"E12.3.46.0"),sQuery(id+"F0.wireOp",EDGE,"E12.6.46.0"),sQuery(id+"F0.wireOp",EDGE,"E12.2.47.0"),sQuery(id+"F0.wireOp",EDGE,"E12.3.47.0"),sQuery(id+"F0.wireOp",EDGE,"E12.6.47.0"),sQuery(id+"F0.wireOp",EDGE,"E12.2.48.0"),sQuery(id+"F0.wireOp",EDGE,"E12.3.48.0"),sQuery(id+"F0.wireOp",EDGE,"E12.6.48.0"),sQuery(id+"F0.wireOp",EDGE,"E12.2.49.0"),sQuery(id+"F0.wireOp",EDGE,"E12.3.49.0"),sQuery(id+"F0.wireOp",EDGE,"E12.6.49.0"),sQuery(id+"F0.wireOp",EDGE,"E12.2.50.0"),sQuery(id+"F0.wireOp",EDGE,"E12.3.50.0"),sQuery(id+"F0.wireOp",EDGE,"E12.6.50.0"),sQuery(id+"F0.wireOp",EDGE,"E12.2.51.0"),sQuery(id+"F0.wireOp",EDGE,"E12.3.51.0"),sQuery(id+"F0.wireOp",EDGE,"E12.6.51.0"),sQuery(id+"F0.wireOp",EDGE,"E12.2.52.0"),sQuery(id+"F0.wireOp",EDGE,"E12.3.52.0"),sQuery(id+"F0.wireOp",EDGE,"E12.6.52.0"),sQuery(id+"F0.wireOp",EDGE,"E12.2.53.0"),sQuery(id+"F0.wireOp",EDGE,"E12.3.53.0"),sQuery(id+"F0.wireOp",EDGE,"E12.6.53.0"),sQuery(id+"F0.wireOp",EDGE,"E12.2.54.0"),sQuery(id+"F0.wireOp",EDGE,"E12.3.54.0"),sQuery(id+"F0.wireOp",EDGE,"E12.6.54.0"),sQuery(id+"F0.wireOp",EDGE,"E12.2.55.0"),sQuery(id+"F0.wireOp",EDGE,"E12.3.55.0"),sQuery(id+"F0.wireOp",EDGE,"E12.6.55.0"),sQuery(id+"F0.wireOp",EDGE,"E12.2.56.0"),sQuery(id+"F0.wireOp",EDGE,"E12.3.56.0"),sQuery(id+"F0.wireOp",EDGE,"E12.6.56.0"),sQuery(id+"F0.wireOp",EDGE,"E12.2.57.0"),sQuery(id+"F0.wireOp",EDGE,"E12.3.57.0"),sQuery(id+"F0.wireOp",EDGE,"E12.6.57.0"),sQuery(id+"F0.wireOp",EDGE,"E12.2.58.0"),sQuery(id+"F0.wireOp",EDGE,"E12.3.58.0"),sQuery(id+"F0.wireOp",EDGE,"E12.6.58.0"),sQuery(id+"F0.wireOp",EDGE,"E12.2.59.0"),sQuery(id+"F0.wireOp",EDGE,"E12.3.59.0"),sQuery(id+"F0.wireOp",EDGE,"E12.6.59.0"),sQuery(id+"F0.wireOp",EDGE,"E13.2.60.0"),sQuery(id+"F0.wireOp",EDGE,"E13.3.60.0"),sQuery(id+"F0.wireOp",EDGE,"E13.6.60.0"),sQuery(id+"F0.wireOp",EDGE,"E13.2.61.0"),sQuery(id+"F0.wireOp",EDGE,"E13.3.61.0"),sQuery(id+"F0.wireOp",EDGE,"E13.6.61.0"),sQuery(id+"F0.wireOp",EDGE,"E13.2.62.0"),sQuery(id+"F0.wireOp",EDGE,"E13.3.62.0"),sQuery(id+"F0.wireOp",EDGE,"E13.6.62.0"),sQuery(id+"F0.wireOp",EDGE,"E13.2.63.0"),sQuery(id+"F0.wireOp",EDGE,"E13.3.63.0"),sQuery(id+"F0.wireOp",EDGE,"E13.6.63.0"),sQuery(id+"F0.wireOp",EDGE,"E13.2.64.0"),sQuery(id+"F0.wireOp",EDGE,"E13.3.64.0"),sQuery(id+"F0.wireOp",EDGE,"E13.6.64.0"),sQuery(id+"F0.wireOp",EDGE,"E13.2.65.0"),sQuery(id+"F0.wireOp",EDGE,"E13.3.65.0"),sQuery(id+"F0.wireOp",EDGE,"E13.6.65.0"),sQuery(id+"F0.wireOp",EDGE,"E13.2.66.0"),sQuery(id+"F0.wireOp",EDGE,"E13.3.66.0"),sQuery(id+"F0.wireOp",EDGE,"E13.6.66.0"),sQuery(id+"F0.wireOp",EDGE,"E13.2.67.0"),sQuery(id+"F0.wireOp",EDGE,"E13.3.67.0"),sQuery(id+"F0.wireOp",EDGE,"E13.6.67.0"),sQuery(id+"F0.wireOp",EDGE,"E13.2.68.0"),sQuery(id+"F0.wireOp",EDGE,"E13.3.68.0"),sQuery(id+"F0.wireOp",EDGE,"E13.6.68.0"),sQuery(id+"F0.wireOp",EDGE,"E13.2.69.0"),sQuery(id+"F0.wireOp",EDGE,"E13.3.69.0"),sQuery(id+"F0.wireOp",EDGE,"E13.6.69.0"),sQuery(id+"F0.wireOp",EDGE,"E13.2.70.0"),sQuery(id+"F0.wireOp",EDGE,"E13.3.70.0"),sQuery(id+"F0.wireOp",EDGE,"E13.6.70.0"),sQuery(id+"F0.wireOp",EDGE,"E13.2.71.0"),sQuery(id+"F0.wireOp",EDGE,"E13.3.71.0"),sQuery(id+"F0.wireOp",EDGE,"E13.6.71.0"),sQuery(id+"F0.wireOp",EDGE,"E13.2.72.0"),sQuery(id+"F0.wireOp",EDGE,"E13.3.72.0"),sQuery(id+"F0.wireOp",EDGE,"E13.6.72.0"),sQuery(id+"F0.wireOp",EDGE,"E13.2.73.0"),sQuery(id+"F0.wireOp",EDGE,"E13.3.73.0"),sQuery(id+"F0.wireOp",EDGE,"E13.6.73.0"),sQuery(id+"F0.wireOp",EDGE,"E13.2.74.0"),sQuery(id+"F0.wireOp",EDGE,"E13.3.74.0"),sQuery(id+"F0.wireOp",EDGE,"E13.6.74.0"),sQuery(id+"F0.wireOp",EDGE,"E13.2.75.0"),sQuery(id+"F0.wireOp",EDGE,"E13.3.75.0"),sQuery(id+"F0.wireOp",EDGE,"E13.6.75.0"),sQuery(id+"F0.wireOp",EDGE,"E13.2.76.0"),sQuery(id+"F0.wireOp",EDGE,"E13.3.76.0"),sQuery(id+"F0.wireOp",EDGE,"E13.6.76.0"),sQuery(id+"F0.wireOp",EDGE,"E13.2.77.0"),sQuery(id+"F0.wireOp",EDGE,"E13.3.77.0"),sQuery(id+"F0.wireOp",EDGE,"E13.6.77.0"),sQuery(id+"F0.wireOp",EDGE,"E13.2.78.0"),sQuery(id+"F0.wireOp",EDGE,"E13.3.78.0"),sQuery(id+"F0.wireOp",EDGE,"E13.6.78.0"),sQuery(id+"F0.wireOp",EDGE,"E13.2.79.0"),sQuery(id+"F0.wireOp",EDGE,"E13.3.79.0"),sQuery(id+"F0.wireOp",EDGE,"E13.6.79.0"),sQuery(id+"F0.wireOp",EDGE,"E13.2.80.0"),sQuery(id+"F0.wireOp",EDGE,"E13.3.80.0"),sQuery(id+"F0.wireOp",EDGE,"E13.6.80.0"),sQuery(id+"F0.wireOp",EDGE,"E13.2.81.0"),sQuery(id+"F0.wireOp",EDGE,"E13.3.81.0"),sQuery(id+"F0.wireOp",EDGE,"E13.6.81.0"),sQuery(id+"F0.wireOp",EDGE,"E13.2.82.0"),sQuery(id+"F0.wireOp",EDGE,"E13.3.82.0"),sQuery(id+"F0.wireOp",EDGE,"E13.6.82.0"),sQuery(id+"F0.wireOp",EDGE,"E13.2.83.0"),sQuery(id+"F0.wireOp",EDGE,"E13.3.83.0"),sQuery(id+"F0.wireOp",EDGE,"E13.6.83.0"),sQuery(id+"F0.wireOp",EDGE,"E13.2.84.0"),sQuery(id+"F0.wireOp",EDGE,"E13.3.84.0"),sQuery(id+"F0.wireOp",EDGE,"E13.6.84.0"),sQuery(id+"F0.wireOp",EDGE,"E13.2.85.0"),sQuery(id+"F0.wireOp",EDGE,"E13.3.85.0"),sQuery(id+"F0.wireOp",EDGE,"E13.6.85.0"),sQuery(id+"F0.wireOp",EDGE,"E13.2.86.0"),sQuery(id+"F0.wireOp",EDGE,"E13.3.86.0"),sQuery(id+"F0.wireOp",EDGE,"E13.6.86.0"),sQuery(id+"F0.wireOp",EDGE,"E13.2.87.0"),sQuery(id+"F0.wireOp",EDGE,"E13.3.87.0"),sQuery(id+"F0.wireOp",EDGE,"E13.6.87.0"),sQuery(id+"F0.wireOp",EDGE,"E13.2.88.0"),sQuery(id+"F0.wireOp",EDGE,"E13.3.88.0"),sQuery(id+"F0.wireOp",EDGE,"E13.6.88.0"),sQuery(id+"F0.wireOp",EDGE,"E13.2.89.0"),sQuery(id+"F0.wireOp",EDGE,"E13.3.89.0"),sQuery(id+"F0.wireOp",EDGE,"E13.6.89.0"),sQuery(id+"F0.wireOp",EDGE,"E13.2.90.0"),sQuery(id+"F0.wireOp",EDGE,"E13.3.90.0"),sQuery(id+"F0.wireOp",EDGE,"E13.6.90.0"),sQuery(id+"F0.wireOp",EDGE,"E13.2.91.0"),sQuery(id+"F0.wireOp",EDGE,"E13.3.91.0"),sQuery(id+"F0.wireOp",EDGE,"E13.6.91.0"),sQuery(id+"F0.wireOp",EDGE,"E13.2.92.0"),sQuery(id+"F0.wireOp",EDGE,"E13.3.92.0"),sQuery(id+"F0.wireOp",EDGE,"E13.6.92.0"),sQuery(id+"F0.wireOp",EDGE,"E13.2.93.0"),sQuery(id+"F0.wireOp",EDGE,"E13.3.93.0"),sQuery(id+"F0.wireOp",EDGE,"E13.6.93.0"),sQuery(id+"F0.wireOp",EDGE,"E13.2.94.0"),sQuery(id+"F0.wireOp",EDGE,"E13.3.94.0"),sQuery(id+"F0.wireOp",EDGE,"E13.6.94.0"),sQuery(id+"F0.wireOp",EDGE,"E13.2.95.0"),sQuery(id+"F0.wireOp",EDGE,"E13.3.95.0"),sQuery(id+"F0.wireOp",EDGE,"E13.6.95.0"),sQuery(id+"F0.wireOp",EDGE,"E13.2.96.0"),sQuery(id+"F0.wireOp",EDGE,"E13.3.96.0"),sQuery(id+"F0.wireOp",EDGE,"E13.6.96.0"),sQuery(id+"F0.wireOp",EDGE,"E13.2.97.0"),sQuery(id+"F0.wireOp",EDGE,"E13.3.97.0"),sQuery(id+"F0.wireOp",EDGE,"E13.6.97.0"),sQuery(id+"F0.wireOp",EDGE,"E13.2.98.0"),sQuery(id+"F0.wireOp",EDGE,"E13.3.98.0"),sQuery(id+"F0.wireOp",EDGE,"E13.6.98.0"),sQuery(id+"F0.wireOp",EDGE,"E13.2.99.0"),sQuery(id+"F0.wireOp",EDGE,"E13.3.99.0"),sQuery(id+"F0.wireOp",EDGE,"E13.6.99.0"),sQuery(id+"F0.wireOp",EDGE,"E13.2.100.0"),sQuery(id+"F0.wireOp",EDGE,"E13.3.100.0"),sQuery(id+"F0.wireOp",EDGE,"E13.6.100.0"),sQuery(id+"F0.wireOp",EDGE,"E13.2.101.0"),sQuery(id+"F0.wireOp",EDGE,"E13.3.101.0"),sQuery(id+"F0.wireOp",EDGE,"E13.6.101.0"),sQuery(id+"F0.wireOp",EDGE,"E13.2.102.0"),sQuery(id+"F0.wireOp",EDGE,"E13.3.102.0"),sQuery(id+"F0.wireOp",EDGE,"E13.6.102.0"),sQuery(id+"F0.wireOp",EDGE,"E13.2.103.0"),sQuery(id+"F0.wireOp",EDGE,"E13.3.103.0"),sQuery(id+"F0.wireOp",EDGE,"E13.6.103.0"),sQuery(id+"F0.wireOp",EDGE,"E13.2.104.0"),sQuery(id+"F0.wireOp",EDGE,"E13.3.104.0"),sQuery(id+"F0.wireOp",EDGE,"E13.6.104.0"),sQuery(id+"F0.wireOp",EDGE,"E13.2.105.0"),sQuery(id+"F0.wireOp",EDGE,"E13.3.105.0"),sQuery(id+"F0.wireOp",EDGE,"E13.6.105.0"),sQuery(id+"F0.wireOp",EDGE,"E13.2.106.0"),sQuery(id+"F0.wireOp",EDGE,"E13.3.106.0"),sQuery(id+"F0.wireOp",EDGE,"E13.6.106.0"),sQuery(id+"F0.wireOp",EDGE,"E13.2.107.0"),sQuery(id+"F0.wireOp",EDGE,"E13.3.107.0"),sQuery(id+"F0.wireOp",EDGE,"E13.6.107.0"),sQuery(id+"F0.wireOp",EDGE,"E13.2.108.0"),sQuery(id+"F0.wireOp",EDGE,"E13.3.108.0"),sQuery(id+"F0.wireOp",EDGE,"E13.6.108.0"),sQuery(id+"F0.wireOp",EDGE,"E13.2.109.0"),sQuery(id+"F0.wireOp",EDGE,"E13.3.109.0"),sQuery(id+"F0.wireOp",EDGE,"E13.6.109.0"),sQuery(id+"F0.wireOp",EDGE,"E13.2.110.0"),sQuery(id+"F0.wireOp",EDGE,"E13.3.110.0"),sQuery(id+"F0.wireOp",EDGE,"E13.6.110.0"),sQuery(id+"F0.wireOp",EDGE,"E13.2.111.0"),sQuery(id+"F0.wireOp",EDGE,"E13.3.111.0"),sQuery(id+"F0.wireOp",EDGE,"E13.6.111.0"),sQuery(id+"F0.wireOp",EDGE,"E13.2.112.0"),sQuery(id+"F0.wireOp",EDGE,"E13.3.112.0"),sQuery(id+"F0.wireOp",EDGE,"E13.6.112.0"),sQuery(id+"F0.wireOp",EDGE,"E13.2.113.0"),sQuery(id+"F0.wireOp",EDGE,"E13.3.113.0"),sQuery(id+"F0.wireOp",EDGE,"E13.6.113.0"),sQuery(id+"F0.wireOp",EDGE,"E13.2.114.0"),sQuery(id+"F0.wireOp",EDGE,"E13.3.114.0"),sQuery(id+"F0.wireOp",EDGE,"E13.6.114.0"),sQuery(id+"F0.wireOp",EDGE,"E13.2.115.0"),sQuery(id+"F0.wireOp",EDGE,"E13.3.115.0"),sQuery(id+"F0.wireOp",EDGE,"E13.6.115.0"),sQuery(id+"F0.wireOp",EDGE,"E13.2.116.0"),sQuery(id+"F0.wireOp",EDGE,"E13.3.116.0"),sQuery(id+"F0.wireOp",EDGE,"E13.6.116.0"),sQuery(id+"F0.wireOp",EDGE,"E13.2.117.0"),sQuery(id+"F0.wireOp",EDGE,"E13.3.117.0"),sQuery(id+"F0.wireOp",EDGE,"E13.6.117.0"),sQuery(id+"F0.wireOp",EDGE,"E13.2.118.0"),sQuery(id+"F0.wireOp",EDGE,"E13.3.118.0"),sQuery(id+"F0.wireOp",EDGE,"E13.6.118.0"),sQuery(id+"F0.wireOp",EDGE,"E13.2.119.0"),sQuery(id+"F0.wireOp",EDGE,"E13.3.119.0"),sQuery(id+"F0.wireOp",EDGE,"E13.6.119.0"),sQuery(id+"F0.wireOp",EDGE,"E14")])],"isStart":true});
            extrude(context, id + "F3", {"entities" : qUnion([Q0]), "operationType" : NewBodyOperationType.REMOVE, "oppositeDirection" : true, "endBoundEntityFace" : qUnion([Q1]), "depth" : 1 * mm});
        }
    });
